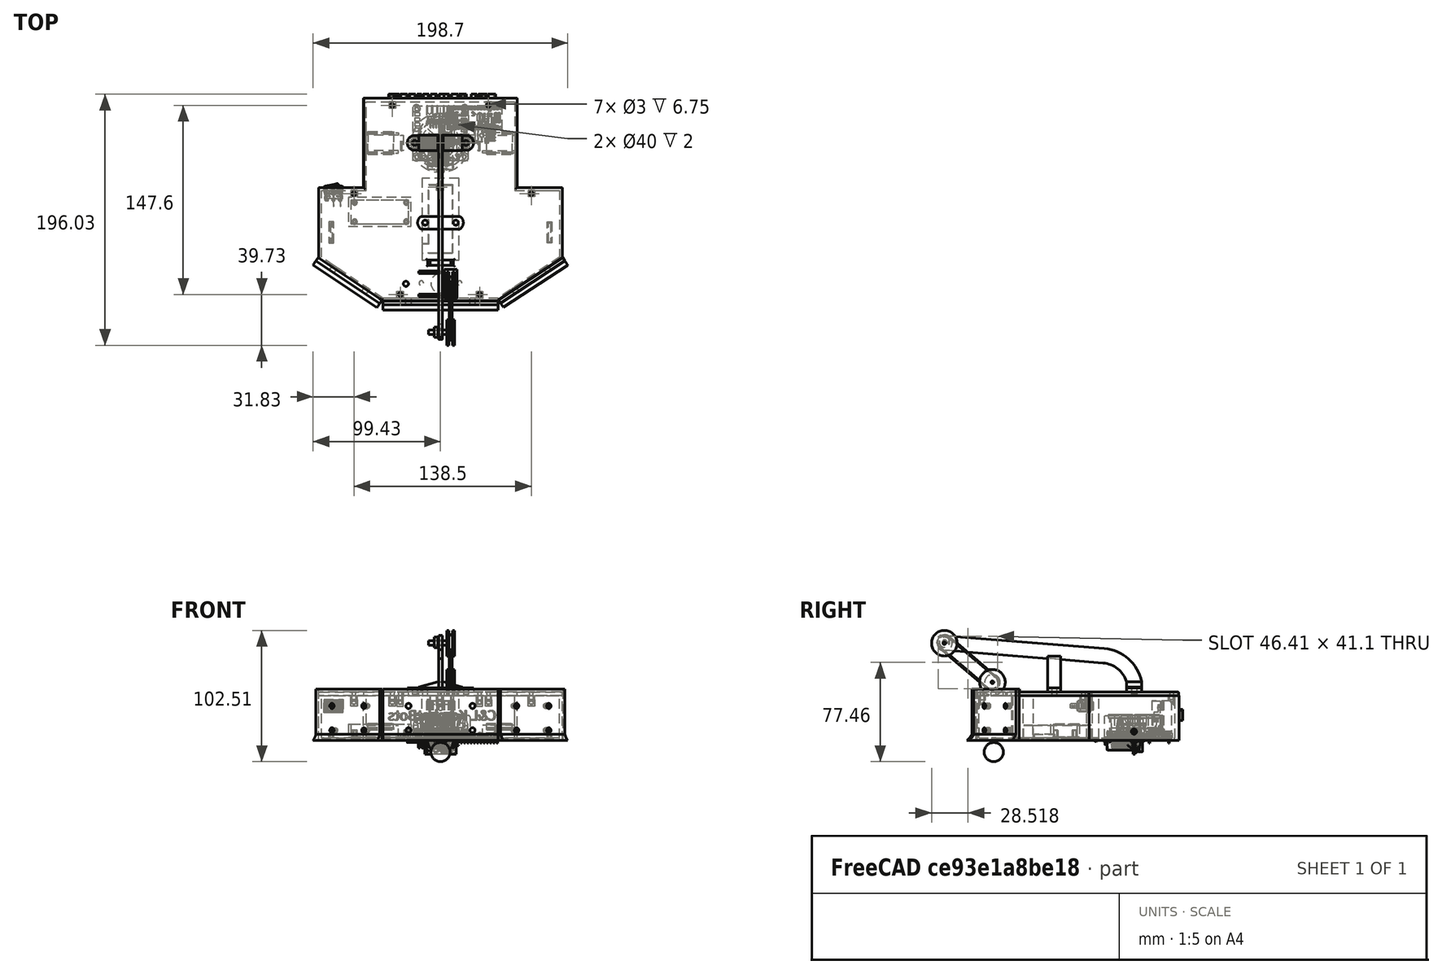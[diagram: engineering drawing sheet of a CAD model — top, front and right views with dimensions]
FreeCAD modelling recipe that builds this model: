
FCSTD DOCUMENT  (FreeCAD 0.20R29410 (Git))
Label: REALSIZEDrobot
License: Creative Commons Attribution-ShareAlike
LicenseURL: http://creativecommons.org/licenses/by-sa/4.0/
objects: Part::Feature×115, Part::Extrusion×50, Sketcher::SketchObject×41, Part::MultiFuse×25, Part::Cut×16, App::Part×9, Part::Chamfer×2, Mesh::Feature×2, Part::Fuse×1, Part::Sphere×1, Part::Part2DObjectPython×1, Part::Fillet×1
note: 253 computed .brp shape members not serialized (recipe doc carries the construction recipe); baked Part::Feature solids carry a one-line shape summary decoded from their .brp

FEATURE [Sketcher::SketchObject] Sketch
  FullyConstrained = true
  sketch-geometry (10):
    g0: LineSegment StartX=-60 StartY=35 StartZ=0 EndX=60 EndY=35 EndZ=0
    g1: LineSegment StartX=60 StartY=35 StartZ=0 EndX=60 EndY=-35 EndZ=0
    g2: LineSegment StartX=60 StartY=-35 StartZ=0 EndX=95 EndY=-35 EndZ=0
    g3: LineSegment StartX=95 StartY=-35 StartZ=0 EndX=95 EndY=-90 EndZ=0
    g4: LineSegment StartX=95 StartY=-90 StartZ=0 EndX=45 EndY=-123.166 EndZ=0
    g5: LineSegment StartX=45 StartY=-123.166 StartZ=0 EndX=-45 EndY=-123.166 EndZ=0
    g6: LineSegment StartX=-45 StartY=-123.166 StartZ=0 EndX=-95 EndY=-90 EndZ=0
    g7: LineSegment StartX=-95 StartY=-90 StartZ=0 EndX=-95 EndY=-35 EndZ=0
    g8: LineSegment StartX=-95 StartY=-35 StartZ=0 EndX=-60 EndY=-35 EndZ=0
    g9: LineSegment StartX=-60 StartY=-35 StartZ=0 EndX=-60 EndY=35 EndZ=0
  constraints (29):
    c: Horizontal(g0)
    c: Coincident(g0,g1)
    c: Vertical(g1)
    c: Coincident(g1,g2)
    c: Coincident(g2,g3)
    c: Coincident(g3,g4)
    c: Coincident(g4,g5)
    c: Coincident(g5,g6)
    c: Coincident(g6,g7)
    c: Coincident(g7,g8)
    c: Horizontal(g8)
    c: Coincident(g8,g9)
    c: Coincident(g9,g0)
    c: DistanceX(g0,g0) = 120
    c: Vertical(g9)
    c: DistanceY(g9,g9) = 70
    c: DistanceX(g8,g8) = 35
    c: Vertical(g7)
    c: DistanceX(g5,g5) = 90
    c: Horizontal(g5)
    c: Vertical(g3)
    c: DistanceY(g3,g3) = 55
    c: Horizontal(g2)
    c: Equal(g2,g8)
    c: Equal(g9,g1)
    c: Distance(g4) = 60
    c: Equal(g4,g6)
    c: Equal(g3,g7)
    c: Symmetric(g1,g0,g-1)
FEATURE [Part::Extrusion] Extrude  label="Floor"
  Base = -> Sketch
  Dir = (0,0,1)
  DirMode = 2
  FaceMakerClass = Part::FaceMakerBullseye
  LengthFwd = 2
  LengthRev = 0
  Solid = true
  Symmetric = false
FEATURE [Sketcher::SketchObject] Sketch001
  FullyConstrained = true
  sketch-geometry (22):
    g0: LineSegment StartX=-60 StartY=35 StartZ=0 EndX=60 EndY=35 EndZ=0
    g1: LineSegment StartX=60 StartY=35 StartZ=0 EndX=60 EndY=-35 EndZ=0
    g2: LineSegment StartX=60 StartY=-35 StartZ=0 EndX=95 EndY=-35 EndZ=0
    g3: LineSegment StartX=95 StartY=-35 StartZ=0 EndX=95 EndY=-90 EndZ=0
    g4: LineSegment StartX=95 StartY=-90 StartZ=0 EndX=45 EndY=-123.166 EndZ=0
    g5: LineSegment StartX=45 StartY=-123.166 StartZ=0 EndX=-45 EndY=-123.166 EndZ=0
    g6: LineSegment StartX=-45 StartY=-123.166 StartZ=0 EndX=-95 EndY=-90 EndZ=0
    g7: LineSegment StartX=-95 StartY=-90 StartZ=0 EndX=-95 EndY=-35 EndZ=0
    g8: LineSegment StartX=-95 StartY=-35 StartZ=0 EndX=-60 EndY=-35 EndZ=0
    g9: LineSegment StartX=-60 StartY=-35 StartZ=0 EndX=-60 EndY=35 EndZ=0
    g10: LineSegment StartX=-58 StartY=32 StartZ=0 EndX=58 EndY=32 EndZ=0
    g11: LineSegment StartX=58 StartY=32 StartZ=0 EndX=58 EndY=-37 EndZ=0
    g12: LineSegment StartX=58 StartY=-37 StartZ=0 EndX=93 EndY=-37 EndZ=0
    g13: LineSegment StartX=93 StartY=-37 StartZ=0 EndX=93 EndY=-89.3266 EndZ=0
    g14: LineSegment StartX=93 StartY=-89.3266 StartZ=0 EndX=45 EndY=-121.166 EndZ=0
    g15: LineSegment StartX=45 StartY=-121.166 StartZ=0 EndX=-45 EndY=-121.166 EndZ=0
    g16: LineSegment StartX=-45 StartY=-121.166 StartZ=0 EndX=-93 EndY=-89.3266 EndZ=0
    g17: LineSegment StartX=-93 StartY=-89.3266 StartZ=0 EndX=-93 EndY=-37 EndZ=0
    g18: LineSegment StartX=-93 StartY=-37 StartZ=0 EndX=-58 EndY=-37 EndZ=0
    g19: LineSegment StartX=-58 StartY=-37 StartZ=0 EndX=-58 EndY=32 EndZ=0
    g20: LineSegment StartX=-45 StartY=-121.166 StartZ=0 EndX=-45 EndY=-123.166 EndZ=0
    g21: LineSegment StartX=45 StartY=-121.166 StartZ=0 EndX=45 EndY=-123.166 EndZ=0
  constraints (63):
    c: Horizontal(g0)
    c: Coincident(g0,g1)
    c: Vertical(g1)
    c: Coincident(g1,g2)
    c: Horizontal(g2)
    c: Coincident(g2,g3)
    c: Vertical(g3)
    c: Coincident(g3,g4)
    c: Coincident(g4,g5)
    c: Horizontal(g5)
    c: Coincident(g5,g6)
    c: Coincident(g6,g7)
    c: Vertical(g7)
    c: Coincident(g7,g8)
    c: Horizontal(g8)
    c: Coincident(g8,g9)
    c: Coincident(g9,g0)
    c: Vertical(g9)
    c: Symmetric(g0,g1,g-1)
    c: DistanceX(g0,g0) = 120
    c: DistanceY(g1,g1) = 70
    c: Equal(g9,g1)
    c: DistanceX(g2,g2) = 35
    c: Equal(g2,g8)
    c: DistanceY(g3,g3) = 55
    c: DistanceX(g5,g5) = 90
    c: Distance(g4) = 60
    c: Equal(g4,g6)
    c: Equal(g3,g7)
    c: Horizontal(g10)
    c: Coincident(g11,g10)
    c: Vertical(g11)
    c: Coincident(g11,g12)
    c: Horizontal(g12)
    c: Coincident(g12,g13)
    c: Vertical(g13)
    c: Coincident(g13,g14)
    c: Coincident(g14,g15)
    c: Horizontal(g15)
    c: Coincident(g15,g16)
    c: Coincident(g16,g17)
    c: Vertical(g17)
    c: Coincident(g17,g18)
    c: Horizontal(g18)
    c: Coincident(g18,g19)
    c: Coincident(g19,g10)
    c: Vertical(g19)
    c: Distance(g10,g0) = 3
    c: Distance(g10,g9) = 2
    c: Distance(g17,g8) = 2
    c: Distance(g16,g7) = 2
    c: Distance(g15,g5) = 2
    c: Distance(g13,g3) = 2
    c: Distance(g12,g2) = 2
    c: Distance(g10,g1) = 2
    c: Coincident(g20,g15)
    c: Coincident(g20,g5)
    c: Coincident(g21,g14)
    c: Coincident(g21,g4)
    c: Vertical(g21)
    c: Vertical(g20)
    c: Parallel(g16,g6)
    c: Parallel(g14,g4)
FEATURE [Part::Extrusion] Extrude001  label="Walls"
  Base = -> Sketch001
  Dir = (0,0,1)
  DirMode = 2
  FaceMakerClass = Part::FaceMakerBullseye
  LengthFwd = 35
  LengthRev = 0
  Solid = true
  Symmetric = false
FEATURE [Part::MultiFuse] Fusion  label="Body"
  Refine = true
  Shapes = -> [Extrude001,Extrude]
FEATURE [Sketcher::SketchObject] Sketch002
  FullyConstrained = false
  MapMode = 5
  Placement = pos=(0,0,2) rot=(0,0,1;0rad)
  Support = -> [Fusion]
  sketch-geometry (36):
    g0: GeomPoint X=25 Y=0 Z=0
    g1: LineSegment StartX=33 StartY=6 StartZ=0 EndX=58 EndY=6 EndZ=0
    g2: LineSegment StartX=58 StartY=6 StartZ=0 EndX=58 EndY=8 EndZ=0
    g3: LineSegment StartX=58 StartY=8 StartZ=0 EndX=33 EndY=8 EndZ=0
    g4: LineSegment StartX=33 StartY=8 StartZ=0 EndX=33 EndY=6 EndZ=0
    g5: GeomPoint X=-25 Y=0 Z=0
    g6: LineSegment StartX=33 StartY=6 StartZ=0 EndX=25 EndY=0 EndZ=0
    g7: GeomPoint X=25 Y=0 Z=0
    g8: LineSegment StartX=32.5993 StartY=-6.5 StartZ=0 EndX=25 EndY=0 EndZ=0
    g9: GeomPoint X=-25 Y=0 Z=0
    g10: GeomPoint X=-25 Y=0 Z=0
    g11: GeomPoint X=25 Y=0 Z=0
    g12: LineSegment StartX=33 StartY=-6 StartZ=0 EndX=58 EndY=-6 EndZ=0
    g13: LineSegment StartX=58 StartY=-6 StartZ=0 EndX=58 EndY=-8 EndZ=0
    g14: LineSegment StartX=58 StartY=-8 StartZ=0 EndX=33 EndY=-8 EndZ=0
    g15: LineSegment StartX=33 StartY=-8 StartZ=0 EndX=33 EndY=-6 EndZ=0
    g16: LineSegment StartX=33 StartY=-6 StartZ=0 EndX=25 EndY=0 EndZ=0
    g17: GeomPoint X=25 Y=0 Z=0
    g18: LineSegment StartX=32.5993 StartY=6.5 StartZ=0 EndX=25 EndY=0 EndZ=0
    g19: GeomPoint X=-25 Y=0 Z=0
    g20: LineSegment StartX=-33 StartY=6 StartZ=0 EndX=-58 EndY=6 EndZ=0
    g21: LineSegment StartX=-58 StartY=6 StartZ=0 EndX=-58 EndY=8 EndZ=0
    g22: LineSegment StartX=-58 StartY=8 StartZ=0 EndX=-33 EndY=8 EndZ=0
    g23: LineSegment StartX=-33 StartY=8 StartZ=0 EndX=-33 EndY=6 EndZ=0
    g24: LineSegment StartX=-33 StartY=6 StartZ=0 EndX=-25 EndY=0 EndZ=0
    g25: GeomPoint X=-25 Y=0 Z=0
    g26: LineSegment StartX=-32.5993 StartY=-6.5 StartZ=0 EndX=-25 EndY=0 EndZ=0
    g27: GeomPoint X=-25 Y=0 Z=0
    g28: LineSegment StartX=-33 StartY=-6 StartZ=0 EndX=-58 EndY=-6 EndZ=0
    g29: LineSegment StartX=-58 StartY=-6 StartZ=0 EndX=-58 EndY=-8 EndZ=0
    g30: LineSegment StartX=-58 StartY=-8 StartZ=0 EndX=-33 EndY=-8 EndZ=0
    g31: LineSegment StartX=-33 StartY=-8 StartZ=0 EndX=-33 EndY=-6 EndZ=0
    g32: LineSegment StartX=-33 StartY=-6 StartZ=0 EndX=-25 EndY=0 EndZ=0
    g33: GeomPoint X=-25 Y=0 Z=0
    g34: LineSegment StartX=-32.5993 StartY=6.5 StartZ=0 EndX=-25 EndY=0 EndZ=0
    g35: LineSegment StartX=-33 StartY=8 StartZ=0 EndX=-33 EndY=-8 EndZ=0
  constraints (60):
    c: PointOnObject(g0,g-1)
    c: Distance(g-1,g0) = 25
    c: Coincident(g1,g2)
    c: Coincident(g2,g3)
    c: Coincident(g3,g4)
    c: Coincident(g4,g1)
    c: Horizontal(g1)
    c: Horizontal(g3)
    c: Vertical(g2)
    c: Vertical(g4)
    c: DistanceY(g4,g4) = 2
    c: DistanceX(g1,g1) = 25
    c: Coincident(g6,g1)
    c: Coincident(g6,g0)
    c: Distance(g6) = 10
    c: DistanceY(g-1,g1) = 6
    c: Coincident(g8,g7)
    c: Distance(g8) = 10
    c: Coincident(g12,g13)
    c: Coincident(g13,g14)
    c: Coincident(g14,g15)
    c: Coincident(g15,g12)
    c: Horizontal(g12)
    c: Horizontal(g14)
    c: Vertical(g13)
    c: Vertical(g15)
    c: Coincident(g16,g12)
    c: Coincident(g16,g11)
    c: Distance(g16) = 10
    c: Coincident(g18,g17)
    c: Distance(g18) = 10
    c: Coincident(g20,g21)
    c: Coincident(g21,g22)
    c: Coincident(g22,g23)
    c: Coincident(g23,g20)
    c: Horizontal(g20)
    c: Horizontal(g22)
    c: Vertical(g21)
    c: Vertical(g23)
    c: Coincident(g24,g20)
    c: Coincident(g24,g19)
    c: Distance(g24) = 10
    c: Coincident(g26,g25)
    c: Distance(g26) = 10
    c: Coincident(g28,g29)
    c: Coincident(g29,g30)
    c: Coincident(g30,g31)
    c: Coincident(g31,g28)
    c: Horizontal(g28)
    c: Horizontal(g30)
    c: Vertical(g29)
    c: Vertical(g31)
    c: Coincident(g32,g28)
    c: Coincident(g32,g27)
    c: Distance(g32) = 10
    c: Coincident(g34,g33)
    c: Distance(g34) = 10
    c: Coincident(g35,g22)
    c: Coincident(g35,g30)
    c: Vertical(g35)
FEATURE [Part::Extrusion] Extrude002  label="motorWalls"
  Base = -> Sketch002
  Dir = (0,0,1)
  DirMode = 2
  FaceMakerClass = Part::FaceMakerBullseye
  LengthFwd = 10
  LengthRev = 0
  Solid = true
  Symmetric = false
FEATURE [Sketcher::SketchObject] Sketch003
  FullyConstrained = false
  MapMode = 5
  Placement = pos=(0,0,2) rot=(0,0,1;0rad)
  Support = -> [Fusion]
  sketch-geometry (10):
    g0: LineSegment StartX=-31 StartY=6 StartZ=0 EndX=-29 EndY=6 EndZ=0
    g1: LineSegment StartX=-29 StartY=6 StartZ=0 EndX=-29 EndY=-6 EndZ=0
    g2: LineSegment StartX=-29 StartY=-6 StartZ=0 EndX=-31 EndY=-6 EndZ=0
    g3: LineSegment StartX=-31 StartY=-6 StartZ=0 EndX=-31 EndY=6 EndZ=0
    g4: GeomPoint X=-30 Y=0 Z=0
    g5: LineSegment StartX=31 StartY=6 StartZ=0 EndX=29 EndY=6 EndZ=0
    g6: LineSegment StartX=29 StartY=6 StartZ=0 EndX=29 EndY=-6 EndZ=0
    g7: LineSegment StartX=29 StartY=-6 StartZ=0 EndX=31 EndY=-6 EndZ=0
    g8: LineSegment StartX=31 StartY=-6 StartZ=0 EndX=31 EndY=6 EndZ=0
    g9: GeomPoint X=30 Y=0 Z=0
  constraints (22):
    c: Coincident(g0,g1)
    c: Coincident(g1,g2)
    c: Coincident(g2,g3)
    c: Coincident(g3,g0)
    c: Horizontal(g0)
    c: Horizontal(g2)
    c: Vertical(g1)
    c: Vertical(g3)
    c: PointOnObject(g4,g-1)
    c: Distance(g-1,g4) = 30
    c: Symmetric(g0,g2,g4)
    c: DistanceX(g0,g0) = 2
    c: DistanceY(g1,g1) = 12
    c: Coincident(g5,g6)
    c: Coincident(g6,g7)
    c: Coincident(g7,g8)
    c: Coincident(g8,g5)
    c: Horizontal(g5)
    c: Horizontal(g7)
    c: Vertical(g6)
    c: Vertical(g8)
    c: Symmetric(g5,g7,g9)
FEATURE [Part::Extrusion] Extrude003
  Base = -> Sketch003
  Dir = (0,0,1)
  DirMode = 2
  FaceMakerClass = Part::FaceMakerBullseye
  LengthFwd = 3
  LengthRev = 0
  Solid = true
  Symmetric = false
FEATURE [Part::Chamfer] Chamfer  label="MotorSlotter"
  Base = -> Extrude003
  Edges = 2 edges r=1: [Edge12,Edge24]
FEATURE [Part::MultiFuse] Fusion001  label="MotorHolders"
  Refine = true
  Shapes = -> [Chamfer,Extrude002]
FEATURE [Part::MultiFuse] Fusion002
  Refine = true
  Shapes = -> [Fusion001,Fusion]
FEATURE [Sketcher::SketchObject] Sketch004
  FullyConstrained = true
  MapMode = 5
  Placement = pos=(0,0,2) rot=(0,0,1;0rad)
  Support = -> [Fusion002]
  sketch-geometry (8):
    g0: Circle CenterX=-18.8 CenterY=26.75 CenterZ=0 NormalX=0 NormalY=0 NormalZ=1 AngleXU=0 Radius=3
    g1: Circle CenterX=-18.8 CenterY=26.75 CenterZ=0 NormalX=0 NormalY=0 NormalZ=1 AngleXU=0 Radius=1.5
    g2: Circle CenterX=18.8 CenterY=26.75 CenterZ=0 NormalX=0 NormalY=0 NormalZ=1 AngleXU=0 Radius=3
    g3: Circle CenterX=18.8 CenterY=26.75 CenterZ=0 NormalX=0 NormalY=0 NormalZ=1 AngleXU=0 Radius=1.5
    g4: Circle CenterX=18.8 CenterY=-11 CenterZ=0 NormalX=0 NormalY=0 NormalZ=1 AngleXU=0 Radius=3
    g5: Circle CenterX=18.8 CenterY=-11 CenterZ=0 NormalX=0 NormalY=0 NormalZ=1 AngleXU=0 Radius=1.5
    g6: Circle CenterX=-18.8 CenterY=-11 CenterZ=0 NormalX=0 NormalY=0 NormalZ=1 AngleXU=0 Radius=3
    g7: Circle CenterX=-18.8 CenterY=-11 CenterZ=0 NormalX=0 NormalY=0 NormalZ=1 AngleXU=0 Radius=1.5
  constraints (20):
    c: Coincident(g1,g0)
    c: Coincident(g3,g2)
    c: Coincident(g5,g4)
    c: Coincident(g7,g6)
    c: DistanceX(g-2,g6) = -18.8
    c: Diameter(g7) = 3
    c: Diameter(g6) = 6
    c: DistanceY(g-1,g6) = -11
    c: DistanceY(g-1,g4) = -11
    c: DistanceX(g-2,g4) = 18.8
    c: Diameter(g5) = 3
    c: Diameter(g4) = 6
    c: DistanceY(g-1,g2) = 26.75
    c: DistanceY(g-1,g0) = 26.75
    c: DistanceX(g-2,g2) = 18.8
    c: DistanceX(g-2,g0) = -18.8
    c: Diameter(g1) = 3
    c: Diameter(g0) = 6
    c: Diameter(g2) = 6
    c: Diameter(g3) = 3
FEATURE [Part::Feature] Part__Feature  label="L298N"
  Placement = pos=(21.5,29,6) rot=(1,0,0;1.5708rad)
  shape: bbox 43 x 43 x 25 mm, 410 faces (baked)
FEATURE [Part::Feature] Part__Feature001  label="Motor Case"
  shape: bbox 14 x 10 x 12 mm, 26 faces (baked)
FEATURE [Part::Feature] Part__Feature002  label="Rear Cover"
  Placement = pos=(7,0,0) rot=(0,0,1;0rad)
  shape: bbox 9 x 10 x 12 mm, 45 faces (baked)
FEATURE [Part::Feature] Part__Feature003  label="Rear Bearing"
  Placement = pos=(8.5,0,0) rot=(1,0,0;0.268142rad)
  shape: bbox 3 x 5 x 5 mm, 9 faces (baked)
FEATURE [Part::Feature] Part__Feature004  label="Front Bearing"
  Placement = pos=(-5.5,-1e-15,0) rot=(0,0,1;0rad)
  shape: bbox 1.5 x 4 x 4 mm, 6 faces (baked)
FEATURE [Part::Feature] Part__Feature005  label="Rotor"
  Placement = pos=(7,-3e-15,0) rot=(1,0,0;0.383419rad)
  shape: bbox 16.7 x 7.6 x 7.6 mm, 34 faces, 3 solids (baked)
FEATURE [Part::Feature] Part__Feature006  label="Spur 1-15_Spur01"
  Placement = pos=(-8.95,-3e-15,0) rot=(0.012886,0.999834,0.012886;1.57096rad)
  shape: bbox 1.5 x 3.391 x 3.382 mm, 38 faces (baked)
FEATURE [Part::Feature] Part__Feature007  label="Plate 1"
  Placement = pos=(-8,-6e-15,6e-15) rot=(0,1,0;1.5708rad)
  shape: bbox 1 x 10 x 12 mm, 14 faces (baked)
FEATURE [Part::Feature] Part__Feature008  label="Stand 2"
  Placement = pos=(-10,3.2,-3.6) rot=(0,0,1;0rad)
  shape: bbox 2 x 3 x 3 mm, 6 faces (baked)
FEATURE [Part::Feature] Part__Feature009  label="Stand 003"
  Placement = pos=(-10,-3.2,3.6) rot=(0,0,1;0rad)
  shape: bbox 2 x 3 x 3 mm, 6 faces (baked)
FEATURE [Part::Feature] Part__Feature010  label="Spur 2-24_Spur01"
  Placement = pos=(-8.95,2.21201,3.21201) rot=(0.153612,-0.976118,-0.153612;1.59497rad)
  shape: bbox 10.4 x 5.193 x 5.193 mm, 56 faces (baked)
FEATURE [Part::Feature] Part__Feature011  label="Plate 2"
  Placement = pos=(-11,-1.9e-14,5e-15) rot=(0,1,0;1.5708rad)
  shape: bbox 1 x 10 x 12 mm, 17 faces (baked)
FEATURE [Part::Feature] Part__Feature012  label="Spur 2-15_Spur01"
  Placement = pos=(-11.2,2.21201,3.21201) rot=(0.392285,0.832,0.392285;1.75369rad)
  shape: bbox 3 x 3.389 x 3.386 mm, 34 faces (baked)
FEATURE [Part::Feature] Part__Feature013  label="Spur 1-26_Spur01"
  Placement = pos=(-11.95,-0.153707,-0.136628) rot=(-0.467826,-0.749852,0.467826;1.85478rad)
  shape: bbox 4.2 x 5.587 x 5.6 mm, 60 faces (baked)
FEATURE [Part::Feature] Part__Feature014  label="Spur 1-15_Spur002"
  Placement = pos=(-13.45,-0.153707,-0.136628) rot=(-0.575214,0.581599,-0.575214;2.08803rad)
  shape: bbox 1.5 x 3.378 x 3.392 mm, 38 faces (baked)
FEATURE [Part::Feature] Part__Feature015  label="Stand 4"
  Placement = pos=(-16.1,3.2,-3.6) rot=(-1,0,0;1.00084rad)
  shape: bbox 5.1 x 3 x 3 mm, 6 faces (baked)
FEATURE [Part::Feature] Part__Feature016  label="Stand 004"
  Placement = pos=(-16.1,-3.2,3.6) rot=(1,0,0;1.52971rad)
  shape: bbox 5.1 x 3 x 3 mm, 6 faces (baked)
FEATURE [Part::Feature] Part__Feature017  label="Spur 1-24_Spur01"
  Placement = pos=(-13.45,-2.35559,-3.35559) rot=(-0.550538,0.627547,-0.550538;2.02074rad)
  shape: bbox 7.1 x 5.2 x 5.2 mm, 56 faces (baked)
FEATURE [Part::Feature] Part__Feature018  label="Plate 3"
  Placement = pos=(-16.1,-2.1e-14,5e-15) rot=(0.707107,0,-0.707107;3.14159rad)
  shape: bbox 2 x 10.2 x 12 mm, 29 faces (baked)
FEATURE [Part::Feature] Part__Feature019  label="Spur 1-15_Spur003"
  Placement = pos=(-15.15,-2.35559,-3.35559) rot=(0.659293,0.361476,0.659293;2.44787rad)
  shape: bbox 1.5 x 3.389 x 3.386 mm, 38 faces (baked)
FEATURE [Part::Feature] Part__Feature020  label="Spur 2-26_Spur01"
  Placement = pos=(-15.15,-2.7e-14,5e-15) rot=(0.080265,0.993537,0.080265;1.57728rad)
  shape: bbox 11.5 x 5.592 x 5.599 mm, 59 faces (baked)
FEATURE [Part::Feature] Part__Feature021  label="countersunk flat head cross recess screw_iso_ISO 7046-1 - M2 x 12 - Z --- 12N"
  Placement = pos=(-17.4,-3.2,3.6) rot=(1,0,0;0.036509rad)
  shape: bbox 12 x 3.8 x 3.8 mm, 41 faces (baked)
FEATURE [Part::Feature] Part__Feature022  label="countersunk flat head cross recess screw_iso_ISO 7046-1 - M2 x 12 - Z --- 12N001"
  Placement = pos=(-17.4,3.2,-3.6) rot=(1,0,0;1.44457rad)
  shape: bbox 12 x 3.8 x 3.8 mm, 41 faces (baked)
FEATURE [App::Part] GA12_N20_Motor_Complet  label="Left Motor"
  Group = -> [Part__Feature001,Part__Feature002,Part__Feature003,Part__Feature004,Part__Feature005,Part__Feature006,Part__Feature007,Part__Feature008,Part__Feature009,Part__Feature010,Part__Feature011,Part__Feature012,Part__Feature013,Part__Feature014,Part__Feature015,Part__Feature016,Part__Feature017,Part__Feature018,Part__Feature019,Part__Feature020,Part__Feature021,Part__Feature022]
  Origin = -> Origin
  Placement = pos=(40,-7.2e-15,7) rot=(0,0.707107,0.707107;3.14159rad)
FEATURE [Part::Feature] Part__Feature023  label="Motor Case001"
  shape: bbox 14 x 10 x 12 mm, 26 faces (baked)
FEATURE [Part::Feature] Part__Feature024  label="Rear Cover001"
  Placement = pos=(7,0,0) rot=(0,0,1;0rad)
  shape: bbox 9 x 10 x 12 mm, 45 faces (baked)
FEATURE [Part::Feature] Part__Feature025  label="Rear Bearing001"
  Placement = pos=(8.5,0,0) rot=(1,0,0;0.268142rad)
  shape: bbox 3 x 5 x 5 mm, 9 faces (baked)
FEATURE [Part::Feature] Part__Feature026  label="Front Bearing001"
  Placement = pos=(-5.5,-1e-15,0) rot=(0,0,1;0rad)
  shape: bbox 1.5 x 4 x 4 mm, 6 faces (baked)
FEATURE [Part::Feature] Part__Feature027  label="Rotor001"
  Placement = pos=(7,-3e-15,0) rot=(1,0,0;0.383419rad)
  shape: bbox 16.7 x 7.6 x 7.6 mm, 34 faces, 3 solids (baked)
FEATURE [Part::Feature] Part__Feature028  label="Spur 1-15_Spur004"
  Placement = pos=(-8.95,-3e-15,0) rot=(0.012886,0.999834,0.012886;1.57096rad)
  shape: bbox 1.5 x 3.391 x 3.382 mm, 38 faces (baked)
FEATURE [Part::Feature] Part__Feature029  label="Plate 004"
  Placement = pos=(-8,-6e-15,6e-15) rot=(0,1,0;1.5708rad)
  shape: bbox 1 x 10 x 12 mm, 14 faces (baked)
FEATURE [Part::Feature] Part__Feature030  label="Stand 005"
  Placement = pos=(-10,3.2,-3.6) rot=(0,0,1;0rad)
  shape: bbox 2 x 3 x 3 mm, 6 faces (baked)
FEATURE [Part::Feature] Part__Feature031  label="Stand 006"
  Placement = pos=(-10,-3.2,3.6) rot=(0,0,1;0rad)
  shape: bbox 2 x 3 x 3 mm, 6 faces (baked)
FEATURE [Part::Feature] Part__Feature032  label="Spur 2-24_Spur002"
  Placement = pos=(-8.95,2.21201,3.21201) rot=(0.153612,-0.976118,-0.153612;1.59497rad)
  shape: bbox 10.4 x 5.193 x 5.193 mm, 56 faces (baked)
FEATURE [Part::Feature] Part__Feature033  label="Plate 005"
  Placement = pos=(-11,-1.9e-14,5e-15) rot=(0,1,0;1.5708rad)
  shape: bbox 1 x 10 x 12 mm, 17 faces (baked)
FEATURE [Part::Feature] Part__Feature034  label="Spur 2-15_Spur002"
  Placement = pos=(-11.2,2.21201,3.21201) rot=(0.392285,0.832,0.392285;1.75369rad)
  shape: bbox 3 x 3.389 x 3.386 mm, 34 faces (baked)
FEATURE [Part::Feature] Part__Feature035  label="Spur 1-26_Spur002"
  Placement = pos=(-11.95,-0.153707,-0.136628) rot=(-0.467826,-0.749852,0.467826;1.85478rad)
  shape: bbox 4.2 x 5.587 x 5.6 mm, 60 faces (baked)
FEATURE [Part::Feature] Part__Feature036  label="Spur 1-15_Spur005"
  Placement = pos=(-13.45,-0.153707,-0.136628) rot=(-0.575214,0.581599,-0.575214;2.08803rad)
  shape: bbox 1.5 x 3.378 x 3.392 mm, 38 faces (baked)
FEATURE [Part::Feature] Part__Feature037  label="Stand 007"
  Placement = pos=(-16.1,3.2,-3.6) rot=(-1,0,0;1.00084rad)
  shape: bbox 5.1 x 3 x 3 mm, 6 faces (baked)
FEATURE [Part::Feature] Part__Feature038  label="Stand 008"
  Placement = pos=(-16.1,-3.2,3.6) rot=(1,0,0;1.52971rad)
  shape: bbox 5.1 x 3 x 3 mm, 6 faces (baked)
FEATURE [Part::Feature] Part__Feature039  label="Spur 1-24_Spur002"
  Placement = pos=(-13.45,-2.35559,-3.35559) rot=(-0.550538,0.627547,-0.550538;2.02074rad)
  shape: bbox 7.1 x 5.2 x 5.2 mm, 56 faces (baked)
FEATURE [Part::Feature] Part__Feature040  label="Plate 006"
  Placement = pos=(-16.1,-2.1e-14,5e-15) rot=(0.707107,0,-0.707107;3.14159rad)
  shape: bbox 2 x 10.2 x 12 mm, 29 faces (baked)
FEATURE [Part::Feature] Part__Feature041  label="Spur 1-15_Spur006"
  Placement = pos=(-15.15,-2.35559,-3.35559) rot=(0.659293,0.361476,0.659293;2.44787rad)
  shape: bbox 1.5 x 3.389 x 3.386 mm, 38 faces (baked)
FEATURE [Part::Feature] Part__Feature042  label="Spur 2-26_Spur002"
  Placement = pos=(-15.15,-2.7e-14,5e-15) rot=(0.080265,0.993537,0.080265;1.57728rad)
  shape: bbox 11.5 x 5.592 x 5.599 mm, 59 faces (baked)
FEATURE [Part::Feature] Part__Feature043  label="countersunk flat head cross recess screw_iso_ISO 7046-1 - M2 x 12 - Z --- 12N002"
  Placement = pos=(-17.4,-3.2,3.6) rot=(1,0,0;0.036509rad)
  shape: bbox 12 x 3.8 x 3.8 mm, 41 faces (baked)
FEATURE [Part::Feature] Part__Feature044  label="countersunk flat head cross recess screw_iso_ISO 7046-1 - M2 x 12 - Z --- 12N003"
  Placement = pos=(-17.4,3.2,-3.6) rot=(1,0,0;1.44457rad)
  shape: bbox 12 x 3.8 x 3.8 mm, 41 faces (baked)
FEATURE [App::Part] GA12_N20_Motor_Complet001  label="Right Motor"
  Group = -> [Part__Feature023,Part__Feature024,Part__Feature025,Part__Feature026,Part__Feature027,Part__Feature028,Part__Feature029,Part__Feature030,Part__Feature031,Part__Feature032,Part__Feature033,Part__Feature034,Part__Feature035,Part__Feature036,Part__Feature037,Part__Feature038,Part__Feature039,Part__Feature040,Part__Feature041,Part__Feature042,Part__Feature043,Part__Feature044]
  Origin = -> Origin001
  Placement = pos=(-40,-1.5e-14,7) rot=(1,0,0;1.5708rad)
FEATURE [Part::Extrusion] Extrude004  label="L289N Holder"
  Base = -> Sketch004
  Dir = (0,0,1)
  DirMode = 2
  FaceMakerClass = Part::FaceMakerBullseye
  LengthFwd = 4
  LengthRev = 0
  Solid = true
  Symmetric = false
FEATURE [Part::MultiFuse] Fusion003
  Refine = true
  Shapes = -> [Extrude004,Fusion002]
FEATURE [Sketcher::SketchObject] Sketch005
  FullyConstrained = true
  MapMode = 5
  Placement = pos=(60,0,0) rot=(0.57735,0.57735,0.57735;2.0944rad)
  Support = -> [Fusion003]
  sketch-geometry (1):
    g0: Circle CenterX=0 CenterY=7 CenterZ=0 NormalX=0 NormalY=0 NormalZ=1 AngleXU=0 Radius=2
  constraints (3):
    c: PointOnObject(g0,g-2)
    c: Diameter(g0) = 4
    c: Distance(g0,g-1) = 7
FEATURE [Sketcher::SketchObject] Sketch006
  FullyConstrained = true
  MapMode = 5
  Placement = pos=(-60,0,0) rot=(0.57735,-0.57735,-0.57735;2.0944rad)
  Support = -> [Fusion003]
  sketch-geometry (1):
    g0: Circle CenterX=0 CenterY=7 CenterZ=0 NormalX=0 NormalY=0 NormalZ=1 AngleXU=0 Radius=2
  constraints (3):
    c: PointOnObject(g0,g-2)
    c: Diameter(g0) = 4
    c: Distance(g-1,g0) = 7
FEATURE [Part::Extrusion] Extrude005
  Base = -> Sketch005
  Dir = (1,0,0)
  DirMode = 2
  FaceMakerClass = Part::FaceMakerBullseye
  LengthFwd = 10
  LengthRev = 0
  Solid = true
  Symmetric = true
FEATURE [Part::Extrusion] Extrude006
  Base = -> Sketch006
  Dir = (-1,0,0)
  DirMode = 2
  FaceMakerClass = Part::FaceMakerBullseye
  LengthFwd = 10
  LengthRev = 0
  Solid = true
  Symmetric = true
FEATURE [Part::MultiFuse] Fusion004  label="Motor Gaps"
  Refine = true
  Shapes = -> [Extrude005,Extrude006]
FEATURE [Part::Cut] Cut
  Base = -> Fusion003
  Refine = true
  Tool = -> Fusion004
FEATURE [Part::Feature] Part__Feature045  label="INTERRUPTOR BASCULANTE"
  Placement = pos=(-83.5,-33.5,27) rot=(0.57735,-0.57735,-0.57735;4.18879rad)
  shape: bbox 15.1 x 17.9 x 10.42 mm, 555 faces, 4 solids (baked)
FEATURE [Sketcher::SketchObject] Sketch007
  FullyConstrained = false
  MapMode = 5
  Placement = pos=(0,-35,0) rot=(0,0.707107,0.707107;3.14159rad)
  Support = -> [Cut]
  sketch-geometry (4):
    g0: LineSegment StartX=90.8327 StartY=31.6367 StartZ=0 EndX=76.0827 EndY=31.6367 EndZ=0
    g1: LineSegment StartX=76.0827 StartY=31.6367 StartZ=0 EndX=76.0827 EndY=21.8867 EndZ=0
    g2: LineSegment StartX=76.0827 StartY=21.8867 StartZ=0 EndX=90.8327 EndY=21.8867 EndZ=0
    g3: LineSegment StartX=90.8327 StartY=21.8867 StartZ=0 EndX=90.8327 EndY=31.6367 EndZ=0
  constraints (8):
    c: Coincident(g0,g1)
    c: Coincident(g1,g2)
    c: Coincident(g2,g3)
    c: Coincident(g3,g0)
    c: Horizontal(g0)
    c: Horizontal(g2)
    c: Vertical(g1)
    c: Vertical(g3)
FEATURE [Part::Extrusion] Extrude007  label="InterruptGap"
  Base = -> Sketch007
  Dir = (0,1,-2e-16)
  DirMode = 2
  FaceMakerClass = Part::FaceMakerBullseye
  LengthFwd = 10
  LengthRev = 0
  Solid = true
  Symmetric = true
FEATURE [Part::Cut] Cut001
  Base = -> Cut
  Refine = true
  Tool = -> Extrude007
FEATURE [Sketcher::SketchObject] Sketch008
  FullyConstrained = false
  MapMode = 5
  Placement = pos=(0,0,2) rot=(0,0,1;0rad)
  Support = -> [Cut001]
  sketch-geometry (20):
    g0: LineSegment StartX=83.4 StartY=-61.75 StartZ=0 EndX=87 EndY=-61.75 EndZ=0
    g1: LineSegment StartX=87 StartY=-61.75 StartZ=0 EndX=87 EndY=-78.25 EndZ=0
    g2: LineSegment StartX=87 StartY=-78.25 StartZ=0 EndX=83.4 EndY=-78.25 EndZ=0
    g3: LineSegment StartX=83.4 StartY=-78.25 StartZ=0 EndX=83.4 EndY=-61.75 EndZ=0
    g4: LineSegment StartX=84.4 StartY=-62.6 StartZ=0 EndX=86 EndY=-62.6 EndZ=0
    g5: LineSegment StartX=86 StartY=-62.6 StartZ=0 EndX=86 EndY=-77.4 EndZ=0
    g6: LineSegment StartX=86 StartY=-77.4 StartZ=0 EndX=84.4 EndY=-77.4 EndZ=0
    g7: LineSegment StartX=84.4 StartY=-77.4 StartZ=0 EndX=84.4 EndY=-62.6 EndZ=0
    g8: GeomPoint X=93 Y=-70 Z=0
    g9: LineSegment StartX=-0.686599 StartY=-70 StartZ=0 EndX=93 EndY=-70 EndZ=0
    g10: LineSegment StartX=-83.4 StartY=-61.75 StartZ=0 EndX=-87 EndY=-61.75 EndZ=0
    g11: LineSegment StartX=-87 StartY=-61.75 StartZ=0 EndX=-87 EndY=-78.25 EndZ=0
    g12: LineSegment StartX=-87 StartY=-78.25 StartZ=0 EndX=-83.4 EndY=-78.25 EndZ=0
    g13: LineSegment StartX=-83.4 StartY=-78.25 StartZ=0 EndX=-83.4 EndY=-61.75 EndZ=0
    g14: LineSegment StartX=-84.4 StartY=-62.6 StartZ=0 EndX=-86 EndY=-62.6 EndZ=0
    g15: LineSegment StartX=-86 StartY=-62.6 StartZ=0 EndX=-86 EndY=-77.4 EndZ=0
    g16: LineSegment StartX=-86 StartY=-77.4 StartZ=0 EndX=-84.4 EndY=-77.4 EndZ=0
    g17: LineSegment StartX=-84.4 StartY=-77.4 StartZ=0 EndX=-84.4 EndY=-62.6 EndZ=0
    g18: GeomPoint X=-93 Y=-70 Z=0
    g19: LineSegment StartX=0.686599 StartY=-70 StartZ=0 EndX=-93 EndY=-70 EndZ=0
  constraints (46):
    c: Coincident(g0,g1)
    c: Coincident(g1,g2)
    c: Coincident(g2,g3)
    c: Coincident(g3,g0)
    c: Horizontal(g0)
    c: Horizontal(g2)
    c: Vertical(g1)
    c: Vertical(g3)
    c: Coincident(g4,g5)
    c: Coincident(g5,g6)
    c: Coincident(g6,g7)
    c: Coincident(g7,g4)
    c: Horizontal(g4)
    c: Horizontal(g6)
    c: Vertical(g7)
    c: DistanceX(g-2,g8) = 93
    c: DistanceY(g-1,g8) = -70
    c: Distance(g8,g1) = 6
    c: Coincident(g9,g8)
    c: Symmetric(g1,g0,g9)
    c: DistanceY(g1,g1) = 16.5
    c: Symmetric(g4,g5,g9)
    c: DistanceY(g5,g5) = 14.8
    c: DistanceX(g0,g0) = 3.6
    c: DistanceX(g4,g4) = 1.6
    c: Distance(g4,g1) = 1
    c: Coincident(g10,g11)
    c: Coincident(g11,g12)
    c: Coincident(g12,g13)
    c: Coincident(g13,g10)
    c: Horizontal(g10)
    c: Horizontal(g12)
    c: Vertical(g11)
    c: Vertical(g13)
    c: Coincident(g14,g15)
    c: Coincident(g15,g16)
    c: Coincident(g16,g17)
    c: Coincident(g17,g14)
    c: Horizontal(g14)
    c: Horizontal(g16)
    c: Vertical(g17)
    c: Distance(g18,g11) = 6
    c: Coincident(g19,g18)
    c: Symmetric(g11,g10,g19)
    c: Symmetric(g14,g15,g19)
    c: Distance(g14,g11) = 1
FEATURE [Part::Extrusion] Extrude008  label="HitSensorHolders"
  Base = -> Sketch008
  Dir = (0,0,1)
  DirMode = 2
  FaceMakerClass = Part::FaceMakerBullseye
  LengthFwd = 3
  LengthRev = 0
  Solid = true
  Symmetric = false
FEATURE [Part::MultiFuse] Fusion005
  Refine = true
  Shapes = -> [Cut001,Extrude008]
FEATURE [Part::Feature] Part__Feature050  label="BAttery"
  Placement = pos=(0,-59.5,2) rot=(0,0,1;0rad)
  shape: bbox 23 x 53 x 10 mm, 8 faces (baked)
FEATURE [Sketcher::SketchObject] Sketch009
  FullyConstrained = true
  sketch-geometry (11):
    g0: LineSegment StartX=-14.5 StartY=-78.5 StartZ=0 EndX=-9.5 EndY=-78.5 EndZ=0
    g1: LineSegment StartX=-9.5 StartY=-78.5 StartZ=0 EndX=-9.5 EndY=-32.5 EndZ=0
    g2: LineSegment StartX=-9.5 StartY=-32.5 StartZ=0 EndX=9.5 EndY=-32.5 EndZ=0
    g3: LineSegment StartX=9.5 StartY=-32.5 StartZ=0 EndX=9.5 EndY=-86.5 EndZ=0
    g4: LineSegment StartX=9.5 StartY=-86.5 StartZ=0 EndX=-14.5 EndY=-86.5 EndZ=0
    g5: LineSegment StartX=-14.5 StartY=-86.5 StartZ=0 EndX=-14.5 EndY=-91.5 EndZ=0
    g6: LineSegment StartX=-14.5 StartY=-91.5 StartZ=0 EndX=14.5 EndY=-91.5 EndZ=0
    g7: LineSegment StartX=14.5 StartY=-91.5 StartZ=0 EndX=14.5 EndY=-27.5 EndZ=0
    g8: LineSegment StartX=14.5 StartY=-27.5 StartZ=0 EndX=-14.5 EndY=-27.5 EndZ=0
    g9: LineSegment StartX=-14.5 StartY=-27.5 StartZ=0 EndX=-14.5 EndY=-78.5 EndZ=0
    g10: GeomPoint X=0 Y=-59.5 Z=0
  constraints (30):
    c: Horizontal(g0)
    c: Coincident(g0,g1)
    c: Vertical(g1)
    c: Coincident(g1,g2)
    c: Horizontal(g2)
    c: Coincident(g2,g3)
    c: Vertical(g3)
    c: Coincident(g3,g4)
    c: Horizontal(g4)
    c: Coincident(g4,g5)
    c: Vertical(g5)
    c: Coincident(g5,g6)
    c: Horizontal(g6)
    c: Coincident(g6,g7)
    c: Vertical(g7)
    c: Coincident(g7,g8)
    c: Horizontal(g8)
    c: Coincident(g8,g9)
    c: Coincident(g9,g0)
    c: Vertical(g9)
    c: DistanceX(g2,g2) = 19
    c: PointOnObject(g10,g-2)
    c: DistanceY(g10,g-1) = 59.5
    c: Symmetric(g3,g1,g10)
    c: Symmetric(g6,g8,g10)
    c: DistanceX(g8,g8) = 29
    c: DistanceY(g3,g3) = 54
    c: DistanceY(g7,g7) = 64
    c: DistanceY(g1,g1) = 46
    c: DistanceX(g6,g6) = 29
FEATURE [Part::Extrusion] Extrude009  label="Battery Gap"
  Base = -> Sketch009
  Dir = (0,0,1)
  DirMode = 2
  FaceMakerClass = Part::FaceMakerBullseye
  LengthFwd = 35
  LengthRev = 0
  Solid = true
  Symmetric = false
FEATURE [Part::MultiFuse] Fusion006
  Refine = true
  Shapes = -> [Extrude009,Fusion005]
FEATURE [Part::Feature] Part__Feature051  label="Arduino Nano"
  Placement = pos=(8.85506,11.9484,3.8e-15) rot=(0,0,1;0rad)
  shape: bbox 43.18 x 18 x 6.8 mm, 962 faces (baked)
FEATURE [Part::Feature] Part__Feature052  label="Mini USB"
  Placement = pos=(8.54506,19.5727,4.14) rot=(0,0,1;0rad)
  shape: bbox 9.5 x 9.7 x 3.9 mm, 197 faces (baked)
FEATURE [Part::Feature] Part__Feature053  label="ATMEGA328P-AU--3DModel-STEP-56544.step.STEP.STEP.STEP"
  Placement = pos=(2.81625,4.09996,0.676804) rot=(1,0,0;1.5708rad)
  shape: bbox 9 x 9 x 1.2 mm, 650 faces, 33 solids (baked)
FEATURE [App::Part] ATMEGA328P_AU_STEP  label="ATMEGA328P-AU.STEP"
  Group = -> [Part__Feature053]
  Origin = -> Origin004
  Placement = pos=(19.8219,24.4243,4.0882) rot=(0,0,1;3.92699rad)
FEATURE [Part::Feature] Part__Feature054  label="CSTCE Crystal"
  Placement = pos=(25.8562,23.1047,4.15) rot=(0,0,-1;0.785398rad)
  shape: bbox 3.182 x 3.182 x 0.71 mm, 47 faces (baked)
FEATURE [Part::Feature] Part__Feature055  label="2Pin Tactile Switch 6x3.6"
  Placement = pos=(30.7142,19.8184,4.14) rot=(0,0,1;1.5708rad)
  shape: bbox 3.633 x 7.9 x 2.2 mm, 48 faces (baked)
FEATURE [Part::Feature] Part__Feature056  label="0603 Resistor"
  Placement = pos=(34.4251,22.4184,4.14) rot=(0,0,1;0rad)
  shape: bbox 1.6 x 0.8 x 0.5 mm, 69 faces (baked)
FEATURE [Part::Feature] Part__Feature057  label="0603 Resistor001"
  Placement = pos=(34.4251,20.7184,4.14) rot=(0,0,1;0rad)
  shape: bbox 1.6 x 0.8 x 0.5 mm, 69 faces (baked)
FEATURE [Part::Feature] Part__Feature058  label="0603 Resistor002"
  Placement = pos=(34.4251,18.9184,4.14) rot=(0,0,1;0rad)
  shape: bbox 1.6 x 0.8 x 0.5 mm, 69 faces (baked)
FEATURE [Part::Feature] Part__Feature059  label="0603 Resistor003"
  Placement = pos=(34.4251,17.2184,4.14) rot=(0,0,1;0rad)
  shape: bbox 1.6 x 0.8 x 0.5 mm, 69 faces (baked)
FEATURE [Part::Feature] Part__Feature060  label="Blue LED"
  Placement = pos=(37.0251,22.4184,4.14) rot=(0,0,1;0rad)
  shape: bbox 1.6 x 0.8 x 0.6 mm, 19 faces (baked)
FEATURE [Part::Feature] Part__Feature061  label="Green LED"
  Placement = pos=(37.0251,20.7184,4.14) rot=(0,0,1;0rad)
  shape: bbox 1.6 x 0.8 x 0.6 mm, 19 faces (baked)
FEATURE [Part::Feature] Part__Feature062  label="Red LED"
  Placement = pos=(37.0251,18.9184,4.14) rot=(0,0,1;0rad)
  shape: bbox 1.6 x 0.8 x 0.6 mm, 19 faces (baked)
FEATURE [Part::Feature] Part__Feature063  label="Blue LED001"
  Placement = pos=(37.0251,17.2184,4.14) rot=(0,0,1;0rad)
  shape: bbox 1.6 x 0.8 x 0.6 mm, 19 faces (baked)
FEATURE [Part::Feature] Part__Feature064  label="Header 2x3"
  Placement = pos=(45.6765,17.0321,4.14) rot=(0,0,1;1.5708rad)
  shape: bbox 5.075 x 7.615 x 10 mm, 168 faces, 6 solids (baked)
FEATURE [Part::Feature] Part__Feature065  label="SOT89"
  Placement = pos=(38.4751,17.3184,0.94) rot=(0,0,1;1.5708rad)
  shape: bbox 7.1 x 6.5 x 1.6 mm, 80 faces (baked)
FEATURE [Part::Feature] Part__Feature066  label="1206 Tantalum"
  Placement = pos=(38.6251,22.3684,2.54) rot=(0,1,0;3.14159rad)
  shape: bbox 3.2 x 1.6 x 1.5 mm, 24 faces (baked)
FEATURE [Part::Feature] Part__Feature067  label="0603 Resistor004"
  Placement = pos=(38.4251,24.9684,2.54) rot=(0,1,0;3.14159rad)
  shape: bbox 1.6 x 0.8 x 0.5 mm, 69 faces (baked)
FEATURE [Part::Feature] Part__Feature068  label="0603 Capacitor"
  Placement = pos=(35.0338,14.4684,2.54) rot=(0,1,0;3.14159rad)
  shape: bbox 1.6 x 0.8 x 0.7 mm, 69 faces (baked)
FEATURE [Part::Feature] Part__Feature069  label="1206 Tantalum001"
  Placement = pos=(7.64506,24.3684,2.54) rot=(1,0,0;3.14159rad)
  shape: bbox 3.2 x 1.6 x 1.5 mm, 24 faces (baked)
FEATURE [Part::Feature] Part__Feature070  label="0603 Capacitor001"
  Placement = pos=(6.90589,22.4745,2.54) rot=(0,1,0;3.14159rad)
  shape: bbox 1.6 x 0.8 x 0.7 mm, 69 faces (baked)
FEATURE [Part::Feature] Part__Feature071  label="0603 Capacitor002"
  Placement = pos=(17.8451,14.0245,2.54) rot=(0,1,0;3.14159rad)
  shape: bbox 1.6 x 0.8 x 0.7 mm, 69 faces (baked)
FEATURE [Part::Feature] Part__Feature072  label="0603 Capacitor003"
  Placement = pos=(17.8451,15.0767,2.54) rot=(0,1,0;3.14159rad)
  shape: bbox 1.6 x 0.8 x 0.7 mm, 69 faces (baked)
FEATURE [Part::Feature] Part__Feature073  label="0603 Capacitor004"
  Placement = pos=(25.3451,21.2855,2.54) rot=(0,1,0;3.14159rad)
  shape: bbox 1.6 x 0.8 x 0.7 mm, 69 faces (baked)
FEATURE [Part::Feature] Part__Feature074  label="0603 Resistor005"
  Placement = pos=(23.8451,15.8601,2.54) rot=(0,1,0;3.14159rad)
  shape: bbox 1.6 x 0.8 x 0.5 mm, 69 faces (baked)
FEATURE [Part::Feature] Part__Feature075  label="0603 Resistor006"
  Placement = pos=(23.8451,14.4709,2.54) rot=(0,1,0;3.14159rad)
  shape: bbox 1.6 x 0.8 x 0.5 mm, 69 faces (baked)
FEATURE [Part::Feature] Part__Feature076  label="CSTCE Crystal001"
  Placement = pos=(13.1731,14.7184,2.53) rot=(0,1,0;3.14159rad)
  shape: bbox 3.2 x 1.35 x 0.71 mm, 47 faces (baked)
FEATURE [Part::Feature] Part__Feature077  label="SOIC16"
  Placement = pos=(16.6451,19.5642,2.54) rot=(0,1,0;3.14159rad)
  shape: bbox 10.2 x 6 x 1.5 mm, 154 faces (baked)
FEATURE [App::Part] Arduino_Nano  label="Arduino Nano001"
  Group = -> [Part__Feature051,Part__Feature052,ATMEGA328P_AU_STEP,Part__Feature054,Part__Feature055,Part__Feature056,Part__Feature057,Part__Feature058,Part__Feature059,Part__Feature060,Part__Feature061,Part__Feature062,Part__Feature063,Part__Feature064,Part__Feature065,Part__Feature066,Part__Feature067,Part__Feature068,Part__Feature069,Part__Feature070,Part__Feature071,Part__Feature072,Part__Feature073,+4 more]
  Origin = -> Origin005
  Placement = pos=(-73.5,-34.5,12.5) rot=(1,0,0;3.14159rad)
FEATURE [Sketcher::SketchObject] Sketch010
  FullyConstrained = false
  MapMode = 5
  Placement = pos=(0,0,2) rot=(0,0,1;0rad)
  Support = -> [Fusion006]
  sketch-geometry (13):
    g0: LineSegment StartX=-52.8 StartY=-54 StartZ=0 EndX=0 EndY=-54 EndZ=0
    g1: LineSegment StartX=-52.8 StartY=-54 StartZ=0 EndX=-84.748 EndY=-54 EndZ=0
    g2: Circle CenterX=-66.9946 CenterY=-46.5 CenterZ=0 NormalX=0 NormalY=0 NormalZ=1 AngleXU=0 Radius=1
    g3: Circle CenterX=-66.9946 CenterY=-46.5 CenterZ=0 NormalX=0 NormalY=0 NormalZ=1 AngleXU=0 Radius=2
    g4: Circle CenterX=-66.9946 CenterY=-61.5 CenterZ=0 NormalX=0 NormalY=0 NormalZ=1 AngleXU=0 Radius=1
    g5: Circle CenterX=-66.9946 CenterY=-61.5 CenterZ=0 NormalX=0 NormalY=0 NormalZ=1 AngleXU=0 Radius=2
    g6: GeomPoint X=-25.3 Y=-54 Z=0
    g7: Circle CenterX=-26.6711 CenterY=-46.5 CenterZ=0 NormalX=0 NormalY=0 NormalZ=1 AngleXU=0 Radius=1
    g8: Circle CenterX=-26.6711 CenterY=-46.5 CenterZ=0 NormalX=0 NormalY=0 NormalZ=1 AngleXU=0 Radius=2
    g9: Circle CenterX=-26.6711 CenterY=-61.5 CenterZ=0 NormalX=0 NormalY=0 NormalZ=1 AngleXU=0 Radius=1
    g10: Circle CenterX=-26.6711 CenterY=-61.5 CenterZ=0 NormalX=0 NormalY=0 NormalZ=1 AngleXU=0 Radius=2
    g11: LineSegment StartX=-52.8 StartY=-54 StartZ=0 EndX=0 EndY=-54 EndZ=0
    g12: GeomPoint X=-25.3 Y=-54 Z=0
  constraints (24):
    c: DistanceY(g0,g-1) = 54
    c: PointOnObject(g0,g-2)
    c: Horizontal(g0)
    c: Coincident(g1,g0)
    c: Horizontal(g1)
    c: Coincident(g3,g2)
    c: Diameter(g2) = 2
    c: Diameter(g3) = 4
    c: Distance(g2,g1) = 7.5
    c: Coincident(g5,g4)
    c: Diameter(g4) = 2
    c: Diameter(g5) = 4
    c: PointOnObject(g6,g0)
    c: DistanceX(g6,g-1) = 25.3
    c: Coincident(g8,g7)
    c: Diameter(g7) = 2
    c: Diameter(g8) = 4
    c: Distance(g7,g0) = 7.5
    c: Horizontal(g11)
    c: PointOnObject(g12,g11)
    c: Coincident(g10,g9)
    c: Diameter(g9) = 2
    c: Diameter(g10) = 4
    c: Distance(g9,g11) = 7.5
FEATURE [Part::Extrusion] Extrude010  label="Arduino Holder"
  Base = -> Sketch010
  Dir = (0,0,1)
  DirMode = 2
  FaceMakerClass = Part::FaceMakerBullseye
  LengthFwd = 6
  LengthRev = 0
  Solid = true
  Symmetric = false
FEATURE [Part::MultiFuse] Fusion007
  Refine = true
  Shapes = -> [Fusion006,Extrude010]
FEATURE [Sketcher::SketchObject] Sketch011
  FullyConstrained = true
  MapMode = 5
  Placement = pos=(0,-91.5,0) rot=(1,0,0;1.5708rad)
  Support = -> [Extrude009]
  sketch-geometry (10):
    g0: LineSegment StartX=8 StartY=35 StartZ=0 EndX=10 EndY=35 EndZ=0
    g1: LineSegment StartX=10 StartY=35 StartZ=0 EndX=10 EndY=2 EndZ=0
    g2: LineSegment StartX=10 StartY=2 StartZ=0 EndX=-10 EndY=2 EndZ=0
    g3: LineSegment StartX=-10 StartY=2 StartZ=0 EndX=-10 EndY=35 EndZ=0
    g4: LineSegment StartX=-10 StartY=35 StartZ=0 EndX=-8 EndY=35 EndZ=0
    g5: LineSegment StartX=-8 StartY=35 StartZ=0 EndX=-8 EndY=4 EndZ=0
    g6: LineSegment StartX=-8 StartY=4 StartZ=0 EndX=8 EndY=4 EndZ=0
    g7: LineSegment StartX=8 StartY=4 StartZ=0 EndX=8 EndY=35 EndZ=0
    g8: GeomPoint X=0 Y=2 Z=0
    g9: LineSegment StartX=0 StartY=2 StartZ=0 EndX=0 EndY=0 EndZ=0
  constraints (28):
    c: Horizontal(g0)
    c: Coincident(g0,g1)
    c: Vertical(g1)
    c: Coincident(g1,g2)
    c: Coincident(g2,g3)
    c: Vertical(g3)
    c: Coincident(g3,g4)
    c: Horizontal(g4)
    c: Coincident(g4,g5)
    c: Vertical(g5)
    c: Coincident(g5,g6)
    c: Horizontal(g6)
    c: Coincident(g6,g7)
    c: Coincident(g7,g0)
    c: Vertical(g7)
    c: DistanceX(g0,g0) = 2
    c: Equal(g4,g0)
    c: DistanceX(g6,g6) = 16
    c: DistanceY(g1,g1) = 33
    c: Equal(g3,g1)
    c: Distance(g6,g2) = 2
    c: Horizontal(g2)
    c: PointOnObject(g8,g2)
    c: DistanceX(g8,g1) = 10
    c: DistanceY(g-1,g1) = 2
    c: Coincident(g9,g8)
    c: Coincident(g9,g-1)
    c: Vertical(g9)
FEATURE [Part::Feature] Part__Feature078  label="Varsayılan"
  shape: bbox 42.6 x 16.1 x 5.9 mm, 343 faces, 7 solids (baked)
FEATURE [App::Part] f818e014b189db61e14b8aa713db12f520221103_1_5sl1wb  label="Bluetooth Module"
  Group = -> [Part__Feature078]
  Origin = -> Origin006
  Placement = pos=(-8,-93,41) rot=(-0.57735,-0.57735,0.57735;4.18879rad)
FEATURE [Part::Extrusion] Extrude011  label="Bluetooth Module Holder"
  Base = -> Sketch011
  Dir = (0,-1,2e-16)
  DirMode = 2
  FaceMakerClass = Part::FaceMakerBullseye
  LengthFwd = 4
  LengthRev = 0
  Solid = true
  Symmetric = false
FEATURE [Part::MultiFuse] Fusion008
  Refine = true
  Shapes = -> [Fusion007,Extrude011]
FEATURE [Sketcher::SketchObject] Sketch012
  FullyConstrained = false
  MapMode = 5
  Placement = pos=(4.907e-13,3.136e-13,35) rot=(0,0,1;0rad)
  Support = -> [Fusion008]
  sketch-geometry (8):
    g0: LineSegment StartX=8 StartY=-92.5 StartZ=0 EndX=8.5 EndY=-92.5 EndZ=0
    g1: LineSegment StartX=8.5 StartY=-92.5 StartZ=0 EndX=8.5 EndY=-94.7 EndZ=0
    g2: LineSegment StartX=8.5 StartY=-94.7 StartZ=0 EndX=8 EndY=-94.7 EndZ=0
    g3: LineSegment StartX=8 StartY=-94.7 StartZ=0 EndX=8 EndY=-92.5 EndZ=0
    g4: LineSegment StartX=-8 StartY=-92.5 StartZ=0 EndX=-8.5 EndY=-92.5 EndZ=0
    g5: LineSegment StartX=-8.5 StartY=-92.5 StartZ=0 EndX=-8.5 EndY=-94.7 EndZ=0
    g6: LineSegment StartX=-8.5 StartY=-94.7 StartZ=0 EndX=-8 EndY=-94.7 EndZ=0
    g7: LineSegment StartX=-8 StartY=-94.7 StartZ=0 EndX=-8 EndY=-92.5 EndZ=0
  constraints (20):
    c: Coincident(g0,g1)
    c: Coincident(g1,g2)
    c: Coincident(g2,g3)
    c: Coincident(g3,g0)
    c: Horizontal(g0)
    c: Horizontal(g2)
    c: Vertical(g1)
    c: Vertical(g3)
    c: DistanceY(g1,g1) = 2.2
    c: DistanceX(g0,g0) = 0.5
    c: DistanceX(g-2,g0) = 8
    c: DistanceY(g-1,g0) = -92.5
    c: Coincident(g4,g5)
    c: Coincident(g5,g6)
    c: Coincident(g6,g7)
    c: Coincident(g7,g4)
    c: Horizontal(g4)
    c: Horizontal(g6)
    c: Vertical(g5)
    c: Vertical(g7)
FEATURE [Part::Extrusion] Extrude012  label="Bluetooth Module Slotter"
  Base = -> Sketch012
  Dir = (1.4e-14,9e-15,1)
  DirMode = 2
  FaceMakerClass = Part::FaceMakerBullseye
  LengthFwd = -32
  LengthRev = 0
  Solid = true
  Symmetric = false
FEATURE [Part::Cut] Cut002
  Base = -> Fusion008
  Refine = true
  Tool = -> Extrude012
FEATURE [Sketcher::SketchObject] Sketch013
  FullyConstrained = false
  MapMode = 5
  Placement = pos=(0,-37,0) rot=(1,0,0;1.5708rad)
  Support = -> [Cut002]
  sketch-geometry (4):
    g0: LineSegment StartX=-91.0267 StartY=31.7549 StartZ=0 EndX=-86.0267 EndY=31.7549 EndZ=0
    g1: LineSegment StartX=-86.0267 StartY=31.7549 StartZ=0 EndX=-86.0267 EndY=26.7549 EndZ=0
    g2: LineSegment StartX=-86.0267 StartY=26.7549 StartZ=0 EndX=-91.0267 EndY=26.7549 EndZ=0
    g3: LineSegment StartX=-91.0267 StartY=26.7549 StartZ=0 EndX=-91.0267 EndY=31.7549 EndZ=0
  constraints (10):
    c: Coincident(g0,g1)
    c: Coincident(g1,g2)
    c: Coincident(g2,g3)
    c: Coincident(g3,g0)
    c: Horizontal(g0)
    c: Horizontal(g2)
    c: Vertical(g1)
    c: Vertical(g3)
    c: DistanceX(g0,g0) = 5
    c: DistanceY(g1,g1) = 5
FEATURE [Part::Extrusion] Extrude013
  Base = -> Sketch013
  Dir = (0,-1,2e-16)
  DirMode = 2
  FaceMakerClass = Part::FaceMakerBullseye
  LengthFwd = 5
  LengthRev = 0
  Solid = true
  Symmetric = false
FEATURE [Part::Chamfer] Chamfer001  label="Bot Screw Holder"
  Base = -> Extrude013
  Edges = 1 edges r=4.99: [Edge10]
FEATURE [Sketcher::SketchObject] Sketch014
  FullyConstrained = true
  MapMode = 5
  Placement = pos=(0,7e-15,31.7549) rot=(0,0,1;0rad)
  Support = -> [Chamfer001]
  sketch-geometry (1):
    g0: Circle CenterX=-88.6 CenterY=-39.7 CenterZ=0 NormalX=0 NormalY=0 NormalZ=1 AngleXU=0 Radius=1.5
  constraints (3):
    c: Diameter(g0) = 3
    c: DistanceX(g-2,g0) = -88.6
    c: DistanceY(g-1,g0) = -39.7
FEATURE [Part::Extrusion] Extrude014  label="Screw Hole"
  Base = -> Sketch014
  Dir = (0,2e-16,1)
  DirMode = 2
  FaceMakerClass = Part::FaceMakerBullseye
  LengthFwd = -8
  LengthRev = 0
  Placement = pos=(0,0,4.5) rot=(0,0,1;0rad)
  Solid = true
  Symmetric = false
FEATURE [Sketcher::SketchObject] Sketch015
  FullyConstrained = false
  MapMode = 5
  Placement = pos=(0,7e-15,31.7549) rot=(0,0,1;0rad)
  Support = -> [Chamfer001]
  sketch-geometry (4):
    g0: LineSegment StartX=-91.0267 StartY=-37 StartZ=0 EndX=-86.0267 EndY=-37 EndZ=0
    g1: LineSegment StartX=-86.0267 StartY=-37 StartZ=0 EndX=-86.0267 EndY=-42 EndZ=0
    g2: LineSegment StartX=-86.0267 StartY=-42 StartZ=0 EndX=-91.0267 EndY=-42 EndZ=0
    g3: LineSegment StartX=-91.0267 StartY=-42 StartZ=0 EndX=-91.0267 EndY=-37 EndZ=0
  constraints (10):
    c: Coincident(g0,g1)
    c: Coincident(g1,g2)
    c: Coincident(g2,g3)
    c: Coincident(g3,g0)
    c: Horizontal(g0)
    c: Horizontal(g2)
    c: Vertical(g1)
    c: Vertical(g3)
    c: DistanceY(g1,g1) = 5
    c: DistanceX(g2,g2) = 5
FEATURE [Part::Extrusion] Extrude015  label="Top Screw Holder"
  Base = -> Sketch015
  Dir = (0,2e-16,1)
  DirMode = 2
  FaceMakerClass = Part::FaceMakerBullseye
  LengthFwd = 3.25
  LengthRev = 0
  Solid = true
  Symmetric = false
FEATURE [Part::Fuse] Fusion009
  Base = -> Chamfer001
  Refine = true
  Tool = -> Extrude015
FEATURE [Part::Cut] Cut003  label="Lid Screw Hole"
  Base = -> Fusion009
  Placement = pos=(21,0,0) rot=(0,0,1;0rad)
  Refine = true
  Tool = -> Extrude014
FEATURE [Part::Feature] Part__Feature079  label="Lid Screw Hole001"
  Placement = pos=(159.5,0,0) rot=(0,0,1;0rad)
  shape: bbox 5 x 5 x 8.25 mm, 13 faces (baked)
FEATURE [Part::Feature] Part__Feature080  label="Lid Screw Hole002"
  Placement = pos=(51,69,0) rot=(0,0,1;0rad)
  shape: bbox 5 x 5 x 8.25 mm, 13 faces (baked)
FEATURE [Part::Feature] Part__Feature081  label="Lid Screw Hole003"
  Placement = pos=(126,69,0) rot=(0,0,1;0rad)
  shape: bbox 5 x 5 x 8.25 mm, 13 faces (baked)
FEATURE [Part::Feature] Part__Feature082  label="Lid Screw Hole004"
  Placement = pos=(-120,-158,0) rot=(0,0,1;3.14159rad)
  shape: bbox 5 x 5 x 8.25 mm, 13 faces (baked)
FEATURE [Part::Feature] Part__Feature083  label="Lid Screw Hole005"
  Placement = pos=(-58,-158,0) rot=(0,0,1;3.14159rad)
  shape: bbox 5 x 5 x 8.25 mm, 13 faces (baked)
FEATURE [Part::Feature] Part__Feature084  label="Lid Screw Hole006"
  Placement = pos=(88,5,0) rot=(0,0,1;0rad)
  shape: bbox 5 x 5 x 8.25 mm, 13 faces (baked)
FEATURE [Part::MultiFuse] Fusion010  label="Lid Screw Holes"
  Refine = true
  Shapes = -> [Cut003,Part__Feature079,Part__Feature080,Part__Feature081,Part__Feature082,Part__Feature083,Part__Feature084]
FEATURE [Part::MultiFuse] Fusion011
  Refine = true
  Shapes = -> [Cut002,Fusion010]
FEATURE [Sketcher::SketchObject] Sketch016
  FullyConstrained = false
  MapMode = 5
  Placement = pos=(70.4856,-106.261,0) rot=(0.919866,0.27735,0.27735;1.65423rad)
  Support = -> [Fusion011]
  sketch-geometry (4):
    g0: Circle CenterX=15 CenterY=27 CenterZ=0 NormalX=0 NormalY=0 NormalZ=1 AngleXU=0 Radius=2
    g1: Circle CenterX=15 CenterY=8 CenterZ=0 NormalX=0 NormalY=0 NormalZ=1 AngleXU=0 Radius=2
    g2: Circle CenterX=-15 CenterY=27 CenterZ=0 NormalX=0 NormalY=0 NormalZ=1 AngleXU=0 Radius=2
    g3: Circle CenterX=-15 CenterY=8 CenterZ=0 NormalX=0 NormalY=0 NormalZ=1 AngleXU=0 Radius=2
  constraints (9):
    c: Diameter(g1) = 4
    c: Diameter(g0) = 4
    c: DistanceX(g-2,g0) = 15
    c: DistanceX(g-2,g1) = 15
    c: Distance(g1,g0) = 19
    c: DistanceY(g-1,g1) = 8
    c: Diameter(g3) = 4
    c: Diameter(g2) = 4
    c: Distance(g3,g2) = 19
FEATURE [Part::Extrusion] Extrude016
  Base = -> Sketch016
  Dir = (0.552771,-0.833333,-5e-16)
  DirMode = 2
  FaceMakerClass = Part::FaceMakerBullseye
  LengthFwd = 10
  LengthRev = 0
  Solid = true
  Symmetric = true
FEATURE [Sketcher::SketchObject] Sketch017
  FullyConstrained = false
  MapMode = 5
  Placement = pos=(-70.4856,-106.261,0) rot=(0.919866,-0.27735,-0.27735;1.65423rad)
  Support = -> [Fusion011]
  sketch-geometry (4):
    g0: Circle CenterX=-15 CenterY=8 CenterZ=0 NormalX=0 NormalY=0 NormalZ=1 AngleXU=0 Radius=2
    g1: Circle CenterX=-15 CenterY=27 CenterZ=0 NormalX=0 NormalY=0 NormalZ=1 AngleXU=0 Radius=2
    g2: Circle CenterX=15 CenterY=8 CenterZ=0 NormalX=0 NormalY=0 NormalZ=1 AngleXU=0 Radius=2
    g3: Circle CenterX=15 CenterY=27 CenterZ=0 NormalX=0 NormalY=0 NormalZ=1 AngleXU=0 Radius=2
  constraints (9):
    c: Diameter(g1) = 4
    c: Distance(g1,g0) = 19
    c: DistanceY(g-1,g0) = 8
    c: DistanceX(g-2,g0) = -15
    c: DistanceX(g-2,g1) = -15
    c: Diameter(g0) = 4
    c: Diameter(g3) = 4
    c: Distance(g3,g2) = 19
    c: Diameter(g2) = 4
FEATURE [Part::Extrusion] Extrude017
  Base = -> Sketch017
  Dir = (-0.552771,-0.833333,0)
  DirMode = 2
  FaceMakerClass = Part::FaceMakerBullseye
  LengthFwd = 10
  LengthRev = 0
  Solid = true
  Symmetric = true
FEATURE [Sketcher::SketchObject] Sketch018
  FullyConstrained = false
  MapMode = 5
  Placement = pos=(0,-123.166,0) rot=(1,0,0;1.5708rad)
  Support = -> [Fusion011]
  sketch-geometry (4):
    g0: Circle CenterX=-25 CenterY=27 CenterZ=0 NormalX=0 NormalY=0 NormalZ=1 AngleXU=0 Radius=2
    g1: Circle CenterX=-25 CenterY=8 CenterZ=0 NormalX=0 NormalY=0 NormalZ=1 AngleXU=0 Radius=2
    g2: Circle CenterX=25 CenterY=27 CenterZ=0 NormalX=0 NormalY=0 NormalZ=1 AngleXU=0 Radius=2
    g3: Circle CenterX=25 CenterY=8 CenterZ=0 NormalX=0 NormalY=0 NormalZ=1 AngleXU=0 Radius=2
  constraints (9):
    c: Equal(g0,g1)
    c: Diameter(g0) = 4
    c: DistanceY(g-1,g1) = 8
    c: Distance(g1,g0) = 19
    c: DistanceX(g-2,g1) = -25
    c: DistanceX(g-2,g0) = -25
    c: Equal(g2,g3)
    c: Diameter(g2) = 4
    c: Distance(g3,g2) = 19
FEATURE [Part::Extrusion] Extrude018
  Base = -> Sketch018
  Dir = (0,-1,2e-16)
  DirMode = 2
  FaceMakerClass = Part::FaceMakerBullseye
  LengthFwd = 10
  LengthRev = 0
  Solid = true
  Symmetric = true
FEATURE [Part::MultiFuse] Fusion012  label="HitPlankScrewHoles"
  Refine = true
  Shapes = -> [Extrude017,Extrude018,Extrude016]
FEATURE [Part::Cut] Cut004  label="Robot Body"
  Base = -> Fusion011
  Refine = true
  Tool = -> Fusion012
FEATURE [Part::Feature] Part__Feature085  label="Center Hit Plank"
  Placement = pos=(-45,-125,20) rot=(0,0,1;0rad)
  shape: bbox 90 x 7 x 40 mm, 11 faces (baked)
FEATURE [Part::Feature] Part__Feature086  label="Right Hit Plank"
  Placement = pos=(46.0783,-123.812,20) rot=(0,0,1;0.580322rad)
  shape: bbox 54.02 x 38.75 x 40 mm, 11 faces (baked)
FEATURE [Part::Feature] Part__Feature087  label="Left Hit Plank"
  Placement = pos=(-96.3708,-90.6732,20) rot=(0,0,-1;0.589049rad)
  shape: bbox 53.78 x 39.15 x 40 mm, 11 faces (baked)
FEATURE [Sketcher::SketchObject] Sketch019
  FullyConstrained = true
  MapMode = 5
  Placement = pos=(0,5.9e-15,26.7549) rot=(1,0,0;3.14159rad)
  Support = -> [Cut004]
  sketch-geometry (4):
    g0: LineSegment StartX=36 StartY=10 StartZ=0 EndX=56 EndY=10 EndZ=0
    g1: LineSegment StartX=56 StartY=10 StartZ=0 EndX=56 EndY=8 EndZ=0
    g2: LineSegment StartX=56 StartY=8 StartZ=0 EndX=36 EndY=8 EndZ=0
    g3: LineSegment StartX=36 StartY=8 StartZ=0 EndX=36 EndY=10 EndZ=0
  constraints (12):
    c: Coincident(g0,g1)
    c: Coincident(g1,g2)
    c: Coincident(g2,g3)
    c: Coincident(g3,g0)
    c: Horizontal(g0)
    c: Horizontal(g2)
    c: Vertical(g1)
    c: Vertical(g3)
    c: DistanceY(g-1,g1) = 8
    c: DistanceY(g1,g1) = 2
    c: DistanceX(g2,g2) = 20
    c: DistanceX(g-2,g2) = 36
FEATURE [Part::Extrusion] Extrude019  label="Motor Holders Lid Slot"
  Base = -> Sketch019
  Dir = (0,-2e-16,-1)
  DirMode = 2
  FaceMakerClass = Part::FaceMakerBullseye
  LengthFwd = 2
  LengthRev = 0
  Placement = pos=(0,1,0) rot=(0,0,1;0rad)
  Solid = true
  Symmetric = false
  TaperAngle = -3
FEATURE [Part::Extrusion] Extrude020  label="Motor Holders Lid Slot001"
  Base = -> Sketch019
  Dir = (0,-2e-16,-1)
  DirMode = 2
  FaceMakerClass = Part::FaceMakerBullseye
  LengthFwd = 2
  LengthRev = 0
  Placement = pos=(-92,17,0) rot=(0,0,1;0rad)
  Solid = true
  Symmetric = false
  TaperAngle = -3
FEATURE [Part::Extrusion] Extrude021  label="Motor Holders Lid Slot002"
  Base = -> Sketch019
  Dir = (0,-2e-16,-1)
  DirMode = 2
  FaceMakerClass = Part::FaceMakerBullseye
  LengthFwd = 2
  LengthRev = 0
  Placement = pos=(0,17,0) rot=(0,0,1;0rad)
  Solid = true
  Symmetric = false
  TaperAngle = -3
FEATURE [Part::Extrusion] Extrude022  label="Motor Holders Lid Slot003"
  Base = -> Sketch019
  Dir = (0,-2e-16,-1)
  DirMode = 2
  FaceMakerClass = Part::FaceMakerBullseye
  LengthFwd = 2
  LengthRev = 0
  Placement = pos=(-92,1,0) rot=(0,0,1;0rad)
  Solid = true
  Symmetric = false
  TaperAngle = -3
FEATURE [Part::MultiFuse] Fusion013  label="Motor Lid Gaps"
  Refine = true
  Shapes = -> [Extrude019,Extrude020,Extrude021,Extrude022]
FEATURE [Part::Cut] Cut005
  Base = -> Cut004
  Refine = true
  Tool = -> Fusion013
FEATURE [Part::Feature] Part__Feature088  label="Left Motor Lid"
  Placement = pos=(-56.5,0,2.5) rot=(0,0,1;0rad)
  shape: bbox 20 x 18 x 5.1 mm, 18 faces (baked)
FEATURE [Part::Feature] Part__Feature089  label="Right Motor Lid"
  Placement = pos=(36,0,2.5) rot=(0,0,1;0rad)
  shape: bbox 20 x 18 x 5.1 mm, 18 faces (baked)
FEATURE [Sketcher::SketchObject] Sketch020
  FullyConstrained = true
  MapMode = 5
  Placement = pos=(0,2.25e-14,31.7549) rot=(1,0,0;3.14159rad)
  Support = -> [Cut005]
  sketch-geometry (8):
    g0: LineSegment StartX=-70 StartY=-44.9 StartZ=0 EndX=-25 EndY=-44.9 EndZ=0
    g1: LineSegment StartX=-25 StartY=-44.9 StartZ=0 EndX=-25 EndY=-63.3 EndZ=0
    g2: LineSegment StartX=-25 StartY=-63.3 StartZ=0 EndX=-70 EndY=-63.3 EndZ=0
    g3: LineSegment StartX=-70 StartY=-63.3 StartZ=0 EndX=-70 EndY=-44.9 EndZ=0
    g4: LineSegment StartX=-72 StartY=-42.9 StartZ=0 EndX=-23 EndY=-42.9 EndZ=0
    g5: LineSegment StartX=-23 StartY=-42.9 StartZ=0 EndX=-23 EndY=-65.3 EndZ=0
    g6: LineSegment StartX=-23 StartY=-65.3 StartZ=0 EndX=-72 EndY=-65.3 EndZ=0
    g7: LineSegment StartX=-72 StartY=-65.3 StartZ=0 EndX=-72 EndY=-42.9 EndZ=0
  constraints (24):
    c: Coincident(g0,g1)
    c: Coincident(g1,g2)
    c: Coincident(g2,g3)
    c: Coincident(g3,g0)
    c: Horizontal(g0)
    c: Horizontal(g2)
    c: Vertical(g1)
    c: Vertical(g3)
    c: Coincident(g4,g5)
    c: Coincident(g5,g6)
    c: Coincident(g6,g7)
    c: Coincident(g7,g4)
    c: Horizontal(g4)
    c: Horizontal(g6)
    c: Vertical(g5)
    c: Vertical(g7)
    c: Distance(g1,g5) = 2
    c: Distance(g1,g6) = 2
    c: Distance(g0,g4) = 2
    c: DistanceY(g-1,g0) = -44.9
    c: DistanceX(g-2,g0) = -25
    c: DistanceX(g0,g0) = 45
    c: DistanceY(g1,g1) = 18.4
    c: Distance(g0,g7) = 2
FEATURE [Part::Extrusion] Extrude023  label="Arduino Walls"
  Base = -> Sketch020
  Dir = (0,-7e-16,-1)
  DirMode = 2
  FaceMakerClass = Part::FaceMakerBullseye
  LengthFwd = 10
  LengthRev = 0
  Placement = pos=(0,-108,-19) rot=(0,0,1;0rad)
  Solid = true
  Symmetric = false
FEATURE [Part::MultiFuse] Fusion014  label="Full Robot Body"
  Refine = true
  Shapes = -> [Cut005,Extrude023]
FEATURE [Part::Sphere] Sphere  label="Marble"
  Angle1 = -90
  Angle2 = 90
  Angle3 = 360
  AttacherType = Attacher::AttachEngine3D
  Placement = pos=(0,-109.5,-9) rot=(0,0,1;0rad)
  Radius = 7.5
FEATURE [Mesh::Feature] Brilliant_Snicket__1_  label="Caster Marble Holder"
  Placement = pos=(-45,-110,4.88e-14) rot=(-1,0,0;3.14159rad)
FEATURE [Sketcher::SketchObject] Sketch024
  FullyConstrained = false
  MapMode = 5
  Placement = pos=(0,0,2) rot=(0,0,1;0rad)
  Support = -> [Fusion014]
  sketch-geometry (2):
    g0: Circle CenterX=15.0092 CenterY=-109.45 CenterZ=0 NormalX=0 NormalY=0 NormalZ=1 AngleXU=0 Radius=1.75
    g1: Circle CenterX=-15.0092 CenterY=-109.45 CenterZ=0 NormalX=0 NormalY=0 NormalZ=1 AngleXU=0 Radius=1.75
  constraints (2):
    c: Diameter(g0) = 3.5
    c: Diameter(g1) = 3.5
FEATURE [Part::Extrusion] Extrude024  label="Idle Wheel Base Screw Hole"
  Base = -> Sketch024
  Dir = (0,0,1)
  DirMode = 2
  FaceMakerClass = Part::FaceMakerBullseye
  LengthFwd = 10
  LengthRev = 0
  Solid = true
  Symmetric = true
FEATURE [Part::Cut] Cut006
  Base = -> Fusion014
  Refine = true
  Tool = -> Extrude024
FEATURE [Part::Part2DObjectPython] ShapeString  # Draft 2D object (typed FeaturePython)
  FontFile = <path>
  MakeFace = true
  Placement = pos=(43.52,35,15.82) rot=(0,0.707107,0.707107;3.14159rad)
  Size = 5
  String = C&L KombatBots
  Tracking = 0
FEATURE [Part::Extrusion] Extrude025  label="RobotText"
  Base = -> ShapeString
  Dir = (1e-16,1,4e-16)
  DirMode = 2
  FaceMakerClass = Part::FaceMakerBullseye
  LengthFwd = 3
  LengthRev = 0
  Solid = false
  Symmetric = false
FEATURE [Part::MultiFuse] Fusion015  label="Full Robot Body001"
  Refine = true
  Shapes = -> [Cut006,Extrude025]
FEATURE [Sketcher::SketchObject] Sketch025
  FullyConstrained = false
  MapMode = 5
  Placement = pos=(0,0,35) rot=(0,0,1;0rad)
  Support = -> [Fusion015]
  sketch-geometry (21):
    g0: LineSegment StartX=-59.987 StartY=34.8273 StartZ=0 EndX=59.8041 EndY=34.8273 EndZ=0
    g1: LineSegment StartX=59.8041 StartY=34.8273 StartZ=0 EndX=59.8041 EndY=-34.9668 EndZ=0
    g2: LineSegment StartX=59.8041 StartY=-34.9668 StartZ=0 EndX=94.9993 EndY=-34.9668 EndZ=0
    g3: LineSegment StartX=94.9993 StartY=-34.9668 StartZ=0 EndX=94.9993 EndY=-89.9973 EndZ=0
    g4: LineSegment StartX=94.9993 StartY=-89.9973 StartZ=0 EndX=44.9644 EndY=-123.178 EndZ=0
    g5: LineSegment StartX=44.9644 StartY=-123.178 StartZ=0 EndX=-45.0068 EndY=-123.178 EndZ=0
    g6: LineSegment StartX=-45.0068 StartY=-123.178 StartZ=0 EndX=-94.9992 EndY=-90.0114 EndZ=0
    g7: LineSegment StartX=-94.9992 StartY=-90.0114 StartZ=0 EndX=-94.9992 EndY=-35.0079 EndZ=0
    g8: LineSegment StartX=-94.9992 StartY=-35.0079 StartZ=0 EndX=-59.987 EndY=-35.0079 EndZ=0
    g9: LineSegment StartX=-59.987 StartY=-35.0079 StartZ=0 EndX=-59.987 EndY=34.8273 EndZ=0
    g10: LineSegment StartX=-9.9591 StartY=-91.5603 StartZ=0 EndX=10.0409 EndY=-91.5603 EndZ=0
    g11: LineSegment StartX=10.0409 StartY=-91.5603 StartZ=0 EndX=10.0409 EndY=-95.5603 EndZ=0
    g12: LineSegment StartX=10.0409 StartY=-95.5603 StartZ=0 EndX=-9.9591 EndY=-95.5603 EndZ=0
    g13: LineSegment StartX=-9.9591 StartY=-95.5603 StartZ=0 EndX=-9.9591 EndY=-91.5603 EndZ=0
    g14: Circle CenterX=37.419 CenterY=29.3 CenterZ=0 NormalX=0 NormalY=0 NormalZ=1 AngleXU=0 Radius=1.5
    g15: Circle CenterX=-37.6122 CenterY=29.279 CenterZ=0 NormalX=0 NormalY=0 NormalZ=1 AngleXU=0 Radius=1.5
    g16: Circle CenterX=-0.59146 CenterY=-34.6907 CenterZ=0 NormalX=0 NormalY=0 NormalZ=1 AngleXU=0 Radius=1.5
    g17: Circle CenterX=70.9045 CenterY=-39.7106 CenterZ=0 NormalX=0 NormalY=0 NormalZ=1 AngleXU=0 Radius=1.5
    g18: Circle CenterX=30.5752 CenterY=-118.304 CenterZ=0 NormalX=0 NormalY=0 NormalZ=1 AngleXU=0 Radius=1.5
    g19: Circle CenterX=-31.3681 CenterY=-118.305 CenterZ=0 NormalX=0 NormalY=0 NormalZ=1 AngleXU=0 Radius=1.5
    g20: Circle CenterX=-67.5923 CenterY=-39.7098 CenterZ=0 NormalX=0 NormalY=0 NormalZ=1 AngleXU=0 Radius=1.5
  constraints (35):
    c: Horizontal(g0)
    c: Coincident(g0,g1)
    c: Vertical(g1)
    c: Coincident(g1,g2)
    c: Horizontal(g2)
    c: Coincident(g2,g3)
    c: Vertical(g3)
    c: Coincident(g3,g4)
    c: Coincident(g4,g5)
    c: Horizontal(g5)
    c: Coincident(g5,g6)
    c: Coincident(g6,g7)
    c: Vertical(g7)
    c: Coincident(g7,g8)
    c: Horizontal(g8)
    c: Coincident(g8,g9)
    c: Coincident(g9,g0)
    c: Vertical(g9)
    c: Coincident(g10,g11)
    c: Coincident(g11,g12)
    c: Coincident(g12,g13)
    c: Coincident(g13,g10)
    c: Horizontal(g10)
    c: Horizontal(g12)
    c: Vertical(g11)
    c: Vertical(g13)
    c: Diameter(g14) = 3
    c: Diameter(g15) = 3
    c: Diameter(g16) = 3
    c: Diameter(g17) = 3
    c: Diameter(g18) = 3
    c: Diameter(g19) = 3
    c: Diameter(g20) = 3
    c: DistanceX(g10,g10) = 20
    c: DistanceY(g11,g11) = 4
FEATURE [Part::Extrusion] Extrude026  label="Lid Base"
  Base = -> Sketch025
  Dir = (0,0,1)
  DirMode = 2
  FaceMakerClass = Part::FaceMakerBullseye
  LengthFwd = 3
  LengthRev = 0
  Solid = true
  Symmetric = false
FEATURE [Part::Feature] Part__Feature090  label="Motor Case002"
  shape: bbox 21.76 x 22.71 x 15.75 mm, 88 faces (baked)
FEATURE [Part::Feature] Part__Feature091  label="Case Permanent Magnets"
  Placement = pos=(-1e-15,-3,-1e-15) rot=(0,0,1;3.14159rad)
  shape: bbox 4.402 x 14 x 14.1 mm, 10 faces (baked)
FEATURE [Part::Feature] Part__Feature092  label="Case Permanent Magnets001"
  Placement = pos=(-2e-16,-17,-2e-16) rot=(0,0,1;0rad)
  shape: bbox 4.402 x 14 x 14.1 mm, 10 faces (baked)
FEATURE [Part::Feature] Part__Feature093  label="Front Shaft  Bearing"
  Placement = pos=(0,-20.5,0) rot=(0,1,0;3.21118rad)
  shape: bbox 5.15 x 1.7 x 5.15 mm, 4 faces (baked)
FEATURE [Part::Feature] Part__Feature094  label="Motor Shaft"
  Placement = pos=(2e-15,-30.4,0) rot=(0,1,0;3.21118rad)
  shape: bbox 2 x 38 x 2 mm, 5 faces (baked)
FEATURE [Part::Feature] Part__Feature095  label="Coil Holder"
  Placement = pos=(-2e-15,-17,2e-15) rot=(0,1,0;1.41703rad)
  shape: bbox 12.8 x 12 x 12.8 mm, 43 faces (baked)
FEATURE [Part::Feature] Part__Feature096  label="Coopper Coil"
  Placement = pos=(-2.67174,-5,-1.42602) rot=(0.518237,-0.604744,0.604744;2.18533rad)
  shape: bbox 2.859 x 13 x 3.277 mm, 46 faces (baked)
FEATURE [Part::Feature] Part__Feature097  label="Coopper Coil001"
  Placement = pos=(-1.81064,-17,5.1534) rot=(-0.994118,-0.07658,-0.07658;1.57669rad)
  shape: bbox 3.277 x 13 x 2.859 mm, 46 faces (baked)
FEATURE [Part::Feature] Part__Feature098  label="Coopper Coil002"
  Placement = pos=(-0.54256,-17,-3.02853) rot=(-0.994118,-0.07658,-0.07658;1.57669rad)
  shape: bbox 3.277 x 13 x 2.859 mm, 46 faces (baked)
FEATURE [Part::Feature] Part__Feature099  label="Coopper Coil003"
  Placement = pos=(5.13223,-17,1.80736) rot=(-0.636447,0.545406,0.545406;2.00801rad)
  shape: bbox 2.859 x 13 x 3.277 mm, 46 faces (baked)
FEATURE [Part::Feature] Part__Feature100  label="Motor Cap"
  Placement = pos=(-2e-15,-3,0) rot=(2e-06,0,1;3.14159rad)
  shape: bbox 20.08 x 9.3 x 15.1 mm, 83 faces (baked)
FEATURE [Part::Feature] Part__Feature101  label="Rear Shaft  Bearing"
  Placement = pos=(-7e-15,4.5,1e-15) rot=(0,1,0;1.64038rad)
  shape: bbox 8 x 2 x 8 mm, 6 faces (baked)
FEATURE [Part::Feature] Part__Feature102  label="Collector Spacer"
  Placement = pos=(-5e-15,2.5,4e-15) rot=(0,1,0;1.41703rad)
  shape: bbox 8 x 0.5 x 8 mm, 4 faces (baked)
FEATURE [Part::Feature] Part__Feature103  label="Shaft Collector Support"
  Placement = pos=(-6e-15,1.5,1e-15) rot=(0,1,0;1.41703rad)
  shape: bbox 4 x 3.5 x 4 mm, 4 faces (baked)
FEATURE [Part::Feature] Part__Feature104  label="Shaft Collector"
  Placement = pos=(-5e-15,-3.23245,1e-15) rot=(0,1,0;1.64038rad)
  shape: bbox 5.971 x 3.5 x 5.971 mm, 24 faces, 4 solids (baked)
FEATURE [Part::Feature] Part__Feature105  label="Collector Cap"
  Placement = pos=(-4.25,-1e-15,7.04998) rot=(0,0,1;0rad)
  shape: bbox 8.5 x 3 x 1.9 mm, 20 faces (baked)
FEATURE [Part::Feature] Part__Feature106  label="Collector Blade"
  Placement = pos=(3.4,1,7.79998) rot=(0,0,1;0rad)
  shape: bbox 5.009 x 1 x 10.54 mm, 14 faces (baked)
FEATURE [Part::Feature] Part__Feature107  label="Collector Blade001"
  Placement = pos=(-3.4,1e-15,7.79998) rot=(0,0,1;3.14159rad)
  shape: bbox 5.009 x 1 x 10.54 mm, 14 faces (baked)
FEATURE [App::Part] Asm2  label="Weapon Motor"
  Group = -> [Part__Feature090,Part__Feature091,Part__Feature092,Part__Feature093,Part__Feature094,Part__Feature095,Part__Feature096,Part__Feature097,Part__Feature098,Part__Feature099,Part__Feature100,Part__Feature101,Part__Feature102,Part__Feature103,Part__Feature104,Part__Feature105,Part__Feature106,Part__Feature107]
  Origin = -> Origin007
  Placement = pos=(-18.25,-110.5,45.5) rot=(0,0,-1;4.71239rad)
FEATURE [Part::Fillet] Fillet
  Base = -> Extrude026
  Edges = 21 edges r=1: [Edge4,Edge7,Edge10,Edge13,Edge16,Edge19,Edge22,Edge25,Edge28,Edge30,Edge34,Edge37,Edge40,Edge42,Edge45,Edge48,Edge51,Edge54,Edge57,Edge60,Edge63]
FEATURE [Sketcher::SketchObject] Sketch026
  FullyConstrained = true
  MapMode = 5
  Placement = pos=(0,0,38) rot=(0,0,1;0rad)
  Support = -> [Fillet]
  sketch-geometry (1):
    g0: Circle CenterX=0 CenterY=-110 CenterZ=0 NormalX=0 NormalY=0 NormalZ=1 AngleXU=0 Radius=2
  constraints (3):
    c: Diameter(g0) = 4
    c: DistanceY(g0,g-1) = 110
    c: PointOnObject(g0,g-2)
FEATURE [Part::Extrusion] Extrude027  label="Weapon Wire slot"
  Base = -> Sketch026
  Dir = (0,0,1)
  DirMode = 2
  FaceMakerClass = Part::FaceMakerBullseye
  LengthFwd = 10
  LengthRev = 0
  Placement = pos=(-27,0,-6.5) rot=(0,0,1;0rad)
  Solid = true
  Symmetric = false
FEATURE [Part::Cut] Cut007
  Base = -> Fillet
  Refine = true
  Tool = -> Extrude027
FEATURE [Sketcher::SketchObject] Sketch028
  FullyConstrained = true
  MapMode = 5
  Placement = pos=(0,0,38) rot=(0,0,1;0rad)
  Support = -> [Cut007]
  sketch-geometry (9):
    g0: LineSegment StartX=-17 StartY=-100 StartZ=0 EndX=0 EndY=-100 EndZ=0
    g1: LineSegment StartX=0 StartY=-100 StartZ=0 EndX=0 EndY=-102 EndZ=0
    g2: LineSegment StartX=0 StartY=-102 StartZ=0 EndX=-17 EndY=-102 EndZ=0
    g3: LineSegment StartX=-17 StartY=-102 StartZ=0 EndX=-17 EndY=-100 EndZ=0
    g4: LineSegment StartX=-17 StartY=-118 StartZ=0 EndX=0 EndY=-118 EndZ=0
    g5: LineSegment StartX=0 StartY=-118 StartZ=0 EndX=0 EndY=-120 EndZ=0
    g6: LineSegment StartX=0 StartY=-120 StartZ=0 EndX=-17 EndY=-120 EndZ=0
    g7: LineSegment StartX=-17 StartY=-120 StartZ=0 EndX=-17 EndY=-118 EndZ=0
    g8: LineSegment StartX=0 StartY=-102 StartZ=0 EndX=0 EndY=-118 EndZ=0
  constraints (26):
    c: Coincident(g0,g1)
    c: Coincident(g1,g2)
    c: Coincident(g2,g3)
    c: Coincident(g3,g0)
    c: Horizontal(g2)
    c: Vertical(g1)
    c: Vertical(g3)
    c: Coincident(g4,g5)
    c: Coincident(g5,g6)
    c: Coincident(g6,g7)
    c: Coincident(g7,g4)
    c: Horizontal(g4)
    c: Horizontal(g6)
    c: Vertical(g5)
    c: Vertical(g7)
    c: Distance(g1,g4) = 16
    c: Distance(g-1,g0) = 100
    c: DistanceX(g0,g0) = 17
    c: DistanceY(g3,g3) = 2
    c: DistanceY(g5,g5) = 2
    c: DistanceX(g6,g6) = 17
    c: Coincident(g8,g1)
    c: Coincident(g8,g4)
    c: Vertical(g8)
    c: DistanceY(g1,g1) = 2
    c: PointOnObject(g0,g-2)
FEATURE [Part::Extrusion] Extrude028  label="Motor Flange Gap"
  Base = -> Sketch028
  Dir = (0,0,1)
  DirMode = 2
  FaceMakerClass = Part::FaceMakerBullseye
  LengthFwd = 10
  LengthRev = 0
  Solid = true
  Symmetric = true
FEATURE [Part::Cut] Cut008
  Base = -> Cut007
  Refine = true
  Tool = -> Extrude028
FEATURE [Sketcher::SketchObject] Sketch030
  FullyConstrained = false
  Placement = pos=(0,0,0) rot=(0.57735,0.57735,0.57735;2.0944rad)
  sketch-geometry (5):
    g0: LineSegment StartX=0 StartY=45.51 StartZ=0 EndX=-34.7613 EndY=45.51 EndZ=0
    g1: Circle CenterX=-18.5 CenterY=45.51 CenterZ=0 NormalX=0 NormalY=0 NormalZ=1 AngleXU=0 Radius=1.1
    g2: Circle CenterX=-18.5 CenterY=45.51 CenterZ=0 NormalX=0 NormalY=0 NormalZ=1 AngleXU=0 Radius=7.5
    g3: LineSegment StartX=-18.5 StartY=45.51 StartZ=0 EndX=-18.5 EndY=53.8942 EndZ=0
    g4: LineSegment StartX=-18.5 StartY=45.51 StartZ=0 EndX=-18.5 EndY=38.7803 EndZ=0
  constraints (12):
    c: PointOnObject(g0,g-2)
    c: Horizontal(g0)
    c: DistanceY(g-1,g0) = 45.51
    c: PointOnObject(g1,g0)
    c: Diameter(g1) = 2.2
    c: Coincident(g2,g1)
    c: Diameter(g2) = 15
    c: Coincident(g3,g1)
    c: Vertical(g3)
    c: Coincident(g4,g1)
    c: Vertical(g4)
    c: DistanceX(g-2,g1) = -18.5
FEATURE [Sketcher::SketchObject] Sketch031
  FullyConstrained = true
  MapMode = 5
  Placement = pos=(6,0,0) rot=(0.57735,0.57735,0.57735;2.0944rad)
  sketch-geometry (2):
    g0: Circle CenterX=-18.5 CenterY=45.51 CenterZ=0 NormalX=0 NormalY=0 NormalZ=1 AngleXU=0 Radius=10
    g1: Circle CenterX=-18.5 CenterY=45.51 CenterZ=0 NormalX=0 NormalY=0 NormalZ=1 AngleXU=0 Radius=6
  constraints (5):
    c: DistanceX(g-2,g0) = -18.5
    c: DistanceY(g-1,g0) = 45.51
    c: Coincident(g1,g0)
    c: Diameter(g0) = 20
    c: Diameter(g1) = 12
FEATURE [Sketcher::SketchObject] Sketch032
  FullyConstrained = false
  MapMode = 5
  Placement = pos=(0,0,38) rot=(0,0,1;0rad)
  Support = -> [Cut008]
  sketch-geometry (8):
    g0: Circle CenterX=-20 CenterY=0 CenterZ=0 NormalX=0 NormalY=0 NormalZ=1 AngleXU=0 Radius=2
    g1: ArcOfCircle CenterX=-20 CenterY=0 CenterZ=0 NormalX=0 NormalY=0 NormalZ=1 AngleXU=0 Radius=5.84308 StartAngle=1.5708 EndAngle=4.71239
    g2: LineSegment StartX=-20 StartY=5.84308 StartZ=0 EndX=0 EndY=5.84308 EndZ=0
    g3: LineSegment StartX=-20 StartY=-5.84308 StartZ=0 EndX=0 EndY=-5.84308 EndZ=0
    g4: Circle CenterX=20 CenterY=0 CenterZ=0 NormalX=0 NormalY=0 NormalZ=1 AngleXU=0 Radius=2
    g5: ArcOfCircle CenterX=20 CenterY=0 CenterZ=0 NormalX=0 NormalY=0 NormalZ=1 AngleXU=0 Radius=5.84308 StartAngle=4.71239 EndAngle=7.85398
    g6: LineSegment StartX=20 StartY=5.84308 StartZ=0 EndX=0 EndY=5.84308 EndZ=0
    g7: LineSegment StartX=20 StartY=-5.84308 StartZ=0 EndX=0 EndY=-5.84308 EndZ=0
  constraints (15):
    c: PointOnObject(g0,g-1)
    c: Diameter(g0) = 4
    c: DistanceX(g0,g-1) = 20
    c: Coincident(g1,g0)
    c: PointOnObject(g2,g-2)
    c: Horizontal(g2)
    c: Horizontal(g3)
    c: Tangent(g1,g3) = -1.5708
    c: Tangent(g1,g2) = 1.5708
    c: Diameter(g4) = 4
    c: Coincident(g5,g4)
    c: Horizontal(g6)
    c: Horizontal(g7)
    c: Tangent(g5,g7) = 1.5708
    c: Tangent(g5,g6) = -1.5708
FEATURE [Part::Extrusion] Extrude031  label="Weapon Base"
  Base = -> Sketch032
  Dir = (0,0,1)
  DirMode = 2
  FaceMakerClass = Part::FaceMakerBullseye
  LengthFwd = 3
  LengthRev = 0
  Solid = true
  Symmetric = false
FEATURE [Sketcher::SketchObject] Sketch033
  FullyConstrained = false
  MapMode = 5
  Placement = pos=(0,0,41) rot=(0,0,1;0rad)
  Support = -> [Extrude031]
  sketch-geometry (2):
    g0: Circle CenterX=19.9922 CenterY=0 CenterZ=0 NormalX=0 NormalY=0 NormalZ=1 AngleXU=0 Radius=2
    g1: Circle CenterX=-19.9922 CenterY=0 CenterZ=0 NormalX=0 NormalY=0 NormalZ=1 AngleXU=0 Radius=2
  constraints (3):
    c: PointOnObject(g0,g-1)
    c: Diameter(g0) = 4
    c: Diameter(g1) = 4
FEATURE [Part::Extrusion] Extrude032  label="Lid Weapon Holes"
  Base = -> Sketch033
  Dir = (0,0,1)
  DirMode = 2
  FaceMakerClass = Part::FaceMakerBullseye
  LengthFwd = 10
  LengthRev = 0
  Solid = true
  Symmetric = true
FEATURE [Part::Cut] Cut010  label="Robot Lid"
  Base = -> Cut008
  Refine = true
  Tool = -> Extrude032
FEATURE [Sketcher::SketchObject] Sketch034
  FullyConstrained = false
  Placement = pos=(0,0,0) rot=(0.57735,0.57735,0.57735;2.0944rad)
  sketch-geometry (9):
    g0: LineSegment StartX=-5.83 StartY=45.92 StartZ=0 EndX=-5.83 EndY=40.92 EndZ=0
    g1: LineSegment StartX=-5.83 StartY=40.92 StartZ=0 EndX=5.83 EndY=40.92 EndZ=0
    g2: LineSegment StartX=5.83 StartY=40.92 StartZ=0 EndX=5.83 EndY=45.92 EndZ=0
    g3: ArcOfCircle CenterX=-25.7931 CenterY=39.7062 CenterZ=0 NormalX=0 NormalY=0 NormalZ=1 AngleXU=0 Radius=20.9078 StartAngle=0.301757 EndAngle=1.49015
    g4: ArcOfCircle CenterX=-25.7931 CenterY=39.7062 CenterZ=0 NormalX=0 NormalY=0 NormalZ=1 AngleXU=0 Radius=32.2278 StartAngle=0.194023 EndAngle=1.49015
    g5: LineSegment StartX=-23.1969 StartY=71.8293 StartZ=0 EndX=-151.498 EndY=82.1987 EndZ=0
    g6: LineSegment StartX=-24.1088 StartY=60.5461 StartZ=0 EndX=-151.69 EndY=70.8573 EndZ=0
    g7: ArcOfCircle CenterX=-143.144 CenterY=76.3844 CenterZ=0 NormalX=0 NormalY=0 NormalZ=1 AngleXU=0 Radius=10.1777 StartAngle=2.53354 EndAngle=3.71567
    g8: Circle CenterX=-143.144 CenterY=76.3844 CenterZ=0 NormalX=0 NormalY=0 NormalZ=1 AngleXU=0 Radius=1.9
  constraints (21):
    c: Coincident(g0,g1)
    c: Coincident(g1,g2)
    c: Horizontal(g1)
    c: Vertical(g0)
    c: Vertical(g2)
    c: Symmetric(g2,g0,g-2)
    c: DistanceY(g0,g0) = 5
    c: Coincident(g3,g0)
    c: Coincident(g4,g3)
    c: Coincident(g4,g2)
    c: DistanceX(g1,g1) = 11.66
    c: Distance(g3,g0) = 20
    c: Distance(g1,g-1) = 40.92
    c: Parallel(g5,g6)
    c: Tangent(g6,g3) = -1.5708
    c: Tangent(g5,g4) = -1.5708
    c: Distance(g3,g4) = 11.32
    c: Coincident(g7,g5)
    c: Coincident(g7,g6)
    c: Coincident(g8,g7)
    c: Diameter(g8) = 3.8
FEATURE [Part::Extrusion] Extrude033  label="Weapon Sling"
  Base = -> Sketch034
  Dir = (1,0,0)
  DirMode = 2
  FaceMakerClass = Part::FaceMakerBullseye
  LengthFwd = 3
  LengthRev = 0
  Solid = true
  Symmetric = true
FEATURE [Part::MultiFuse] Fusion016  label="Weapon Holder"
  Refine = true
  Shapes = -> [Extrude031,Extrude033]
FEATURE [Sketcher::SketchObject] Sketch037
  FullyConstrained = false
  MapMode = 5
  Placement = pos=(-1.5,0,0) rot=(0.57735,-0.57735,-0.57735;2.0944rad)
  Support = -> [Fusion016]
  sketch-geometry (1):
    g0: Circle CenterX=54.8268 CenterY=76.655 CenterZ=0 NormalX=0 NormalY=0 NormalZ=1 AngleXU=0 Radius=1.85
  constraints (1):
    c: Diameter(g0) = 3.7
FEATURE [Part::Extrusion] Extrude036  label="Cilinder Gear"
  Base = -> Sketch037
  Dir = (-1,0,0)
  DirMode = 2
  FaceMakerClass = Part::FaceMakerBullseye
  LengthFwd = 20
  LengthRev = 0
  Placement = pos=(12.3,-93,0) rot=(0,0,1;0rad)
  Solid = true
  Symmetric = false
FEATURE [Sketcher::SketchObject] Sketch039
  FullyConstrained = false
  MapMode = 5
  Placement = pos=(-2,-93,0) rot=(0.57735,-0.57735,-0.57735;2.0944rad)
  sketch-geometry (1):
    g0: Circle CenterX=54.7831 CenterY=76.6691 CenterZ=0 NormalX=0 NormalY=0 NormalZ=1 AngleXU=0 Radius=4
  constraints (1):
    c: Diameter(g0) = 8
FEATURE [Part::Extrusion] Extrude037  label="Kunai Drive Stopper"
  Base = -> Sketch039
  Dir = (-1,0,0)
  DirMode = 2
  FaceMakerClass = Part::FaceMakerBullseye
  LengthFwd = 3
  LengthRev = 0
  Solid = true
  Symmetric = false
FEATURE [Mesh::Feature] Kunai
  Placement = pos=(5.3,-148.1,60.7) rot=(0,1,0;4.71239rad)
FEATURE [Sketcher::SketchObject] Sketch040
  FullyConstrained = false
  Placement = pos=(0,0,0) rot=(0.57735,0.57735,0.57735;2.0944rad)
  sketch-geometry (8):
    g0: ArcOfCircle CenterX=-54.7336 CenterY=76.5245 CenterZ=0 NormalX=0 NormalY=0 NormalZ=1 AngleXU=0 Radius=5 StartAngle=0.86388 EndAngle=4.00547
    g1: ArcOfCircle CenterX=-18.2895 CenterY=45.3946 CenterZ=0 NormalX=0 NormalY=0 NormalZ=1 AngleXU=0 Radius=5 StartAngle=4.00547 EndAngle=7.14707
    g2: LineSegment StartX=-51.4861 StartY=80.3264 StartZ=0 EndX=-15.042 EndY=49.1965 EndZ=0
    g3: LineSegment StartX=-57.9811 StartY=72.7227 StartZ=0 EndX=-21.5369 EndY=41.5928 EndZ=0
    g4: ArcOfCircle CenterX=-54.7336 CenterY=76.5245 CenterZ=0 NormalX=0 NormalY=0 NormalZ=1 AngleXU=0 Radius=6 StartAngle=0.86388 EndAngle=4.00547
    g5: ArcOfCircle CenterX=-18.2895 CenterY=45.3946 CenterZ=0 NormalX=0 NormalY=0 NormalZ=1 AngleXU=0 Radius=6 StartAngle=4.00547 EndAngle=7.14707
    g6: LineSegment StartX=-50.8366 StartY=81.0867 StartZ=0 EndX=-14.3925 EndY=49.9568 EndZ=0
    g7: LineSegment StartX=-58.6305 StartY=71.9623 StartZ=0 EndX=-22.1864 EndY=40.8324 EndZ=0
  constraints (16):
    c: Diameter(g1) = 10
    c: Diameter(g0) = 10
    c: Equal(g3,g2)
    c: Tangent(g0,g2) = 1.5708
    c: Coincident(g1,g2)
    c: Tangent(g1,g3) = -1.5708
    c: Coincident(g4,g0)
    c: Coincident(g5,g1)
    c: Diameter(g4) = 12
    c: Diameter(g5) = 12
    c: Tangent(g5,g7) = -1.5708
    c: Tangent(g5,g6) = 1.5708
    c: PointOnObject(g4,g7)
    c: Tangent(g7,g4) = -1.5708
    c: Tangent(g4,g6) = 1.5708
    c: Tangent(g0,g3) = -1.5708
FEATURE [Part::Extrusion] Extrude038  label="Rubber Band"
  Base = -> Sketch040
  Dir = (1,0,0)
  DirMode = 2
  FaceMakerClass = Part::FaceMakerBullseye
  LengthFwd = 2
  LengthRev = 0
  Placement = pos=(7,-93,0) rot=(0,0,1;0rad)
  Solid = true
  Symmetric = false
FEATURE [Part::Extrusion] Extrude039
  Base = -> Sketch030
  Dir = (1,0,0)
  DirMode = 2
  FaceMakerClass = Part::FaceMakerBullseye
  LengthFwd = 6
  LengthRev = 0
  Solid = true
  Symmetric = false
FEATURE [Part::Extrusion] Extrude040
  Base = -> Sketch031
  Dir = (1,0,0)
  DirMode = 2
  FaceMakerClass = Part::FaceMakerBullseye
  LengthFwd = 3
  LengthRev = 0
  Placement = pos=(-4.5,0,0) rot=(0,0,1;0rad)
  Solid = true
  Symmetric = false
FEATURE [Part::Cut] Cut011  label="Motor Band Gear"
  Base = -> Extrude039
  Placement = pos=(5,-92,0) rot=(0,0,1;0rad)
  Refine = true
  Tool = -> Extrude040
FEATURE [Part::Feature] Part__Feature108  label="Motor Band Gear001"
  Placement = pos=(5,-129.5,31) rot=(0,0,1;0rad)
  shape: bbox 6 x 15 x 15 mm, 8 faces (baked)
FEATURE [Part::Extrusion] Extrude041  label="Cilinder Gear001"
  Base = -> Sketch037
  Dir = (-1,0,0)
  DirMode = 2
  FaceMakerClass = Part::FaceMakerBullseye
  LengthFwd = 15
  LengthRev = 0
  Placement = pos=(12.3,-93,0) rot=(0,0,1;0rad)
  Solid = true
  Symmetric = false
FEATURE [Part::Cut] Cut012  label="Stopper"
  Base = -> Extrude037
  Refine = true
  Tool = -> Extrude041
FEATURE [Part::MultiFuse] Fusion017  label="Kunai Chain gear"
  Placement = pos=(0,0,-0.5) rot=(0,0,1;0rad)
  Refine = true
  Shapes = -> [Part__Feature108,Extrude036]
FEATURE [Part::Feature] Part__Feature109  label="Robot Rim"
  shape: bbox 40 x 40 x 20.01 mm, 43 faces (baked)
FEATURE [Part::Feature] Part__Feature110  label="Robot Tire"
  shape: bbox 49.79 x 49.79 x 19 mm, 10 faces (baked)
FEATURE [App::Part] TIRE  label="Left Tire"
  Group = -> [Part__Feature109,Part__Feature110]
  Origin = -> Origin008
  Placement = pos=(-60.5,0,6.5) rot=(0,1,0;4.71239rad)
FEATURE [Part::Feature] Part__Feature111  label="Robot Rim001"
  shape: bbox 40 x 40 x 20.01 mm, 43 faces (baked)
FEATURE [Part::Feature] Part__Feature112  label="Robot Tire001"
  shape: bbox 49.79 x 49.79 x 19 mm, 10 faces (baked)
FEATURE [App::Part] TIRE001  label="Right Tire"
  Group = -> [Part__Feature111,Part__Feature112]
  Origin = -> Origin009
  Placement = pos=(60.5,2.4e-15,6.5) rot=(-0.707107,0,-0.707107;3.14159rad)
FEATURE [Sketcher::SketchObject] Sketch042
  FullyConstrained = false
  MapMode = 5
  Placement = pos=(0,0,41) rot=(0,0,1;0rad)
  Support = -> [Fusion016]
  sketch-geometry (8):
    g0: LineSegment StartX=1.5 StartY=5.875 StartZ=0 EndX=16.9097 EndY=5.875 EndZ=0
    g1: LineSegment StartX=16.9097 StartY=5.875 StartZ=0 EndX=16.9097 EndY=-5.875 EndZ=0
    g2: LineSegment StartX=16.9097 StartY=-5.875 StartZ=0 EndX=1.5 EndY=-5.875 EndZ=0
    g3: LineSegment StartX=1.5 StartY=-5.875 StartZ=0 EndX=1.5 EndY=5.875 EndZ=0
    g4: LineSegment StartX=-1.5 StartY=5.875 StartZ=0 EndX=-16.9097 EndY=5.875 EndZ=0
    g5: LineSegment StartX=-16.9097 StartY=5.875 StartZ=0 EndX=-16.9097 EndY=-5.875 EndZ=0
    g6: LineSegment StartX=-16.9097 StartY=-5.875 StartZ=0 EndX=-1.5 EndY=-5.875 EndZ=0
    g7: LineSegment StartX=-1.5 StartY=-5.875 StartZ=0 EndX=-1.5 EndY=5.875 EndZ=0
  constraints (19):
    c: Coincident(g0,g1)
    c: Coincident(g1,g2)
    c: Coincident(g2,g3)
    c: Coincident(g3,g0)
    c: Horizontal(g0)
    c: Horizontal(g2)
    c: Vertical(g1)
    c: Vertical(g3)
    c: DistanceY(g1,g1) = 11.75
    c: DistanceY(g-1,g0) = 5.875
    c: DistanceX(g-2,g0) = 1.5
    c: Coincident(g4,g5)
    c: Coincident(g5,g6)
    c: Coincident(g6,g7)
    c: Coincident(g7,g4)
    c: Horizontal(g4)
    c: Horizontal(g6)
    c: Vertical(g5)
    c: Vertical(g7)
FEATURE [Part::Extrusion] Extrude042
  Base = -> Sketch042
  Dir = (0,0,1)
  DirMode = 2
  FaceMakerClass = Part::FaceMakerBullseye
  LengthFwd = 5
  LengthRev = 0
  Solid = true
  Symmetric = false
FEATURE [Sketcher::SketchObject] Sketch043
  FullyConstrained = false
  MapMode = 45
  Placement = pos=(0,-5.875,43.5) rot=(0.57735,0.57735,0.57735;4.18879rad)
  Support = -> [Extrude042]
  sketch-geometry (4):
    g0: LineSegment StartX=3.07193 StartY=-17.6179 StartZ=0 EndX=-1.78812 EndY=-17.6179 EndZ=0
    g1: LineSegment StartX=-1.78812 StartY=-17.6179 StartZ=0 EndX=-1.78812 EndY=-16.8506 EndZ=0
    g2: LineSegment StartX=-1.78812 StartY=-16.8506 StartZ=0 EndX=3.07193 EndY=0 EndZ=0
    g3: LineSegment StartX=3.07193 StartY=0 StartZ=0 EndX=3.07193 EndY=-17.6179 EndZ=0
  constraints (7):
    c: Horizontal(g0)
    c: Coincident(g0,g1)
    c: Vertical(g1)
    c: Coincident(g1,g2)
    c: Coincident(g2,g3)
    c: Vertical(g3)
    c: Coincident(g0,g3)
FEATURE [Part::Extrusion] Extrude043
  Base = -> Sketch043
  Dir = (0,1,0)
  DirMode = 2
  FaceMakerClass = Part::FaceMakerBullseye
  LengthFwd = 100
  LengthRev = 100
  Solid = true
  Symmetric = false
FEATURE [Part::Extrusion] Extrude044
  Base = -> Sketch043
  Dir = (0,1,0)
  DirMode = 2
  FaceMakerClass = Part::FaceMakerBullseye
  LengthFwd = 100
  LengthRev = 100
  Placement = pos=(0,0,0) rot=(0,0,1;3.14159rad)
  Solid = true
  Symmetric = false
FEATURE [Part::MultiFuse] Fusion018  label="Reinforcements Cut"
  Refine = true
  Shapes = -> [Extrude044,Extrude043]
FEATURE [Part::Cut] Cut013  label="Weapon Holder Reinforcement"
  Base = -> Extrude042
  Refine = true
  Tool = -> Fusion018
FEATURE [Part::MultiFuse] Fusion019  label="Weapon Holder001"
  Refine = true
  Shapes = -> [Fusion016,Cut013]
FEATURE [Sketcher::SketchObject] Sketch044
  FullyConstrained = false
  MapMode = 5
  Placement = pos=(-5,0,0) rot=(0.57735,-0.57735,-0.57735;2.0944rad)
  Support = -> [Cut012]
  sketch-geometry (1):
    g0: Circle CenterX=147.795 CenterY=76.6448 CenterZ=0 NormalX=0 NormalY=0 NormalZ=1 AngleXU=0 Radius=1.9
  constraints (1):
    c: Diameter(g0) = 3.8
FEATURE [Part::Extrusion] Extrude045
  Base = -> Sketch044
  Dir = (-1,0,0)
  DirMode = 2
  FaceMakerClass = Part::FaceMakerBullseye
  LengthFwd = 10
  LengthRev = 0
  Solid = true
  Symmetric = true
FEATURE [Sketcher::SketchObject] Sketch045
  FullyConstrained = false
  MapMode = 5
  Placement = pos=(0,0,38) rot=(0,0,1;0rad)
  Support = -> [Cut010]
  sketch-geometry (6):
    g0: LineSegment StartX=-15 StartY=-57.3216 StartZ=0 EndX=15 EndY=-57.3216 EndZ=0
    g1: LineSegment StartX=15 StartY=-67.3216 StartZ=0 EndX=-15 EndY=-67.3216 EndZ=0
    g2: Circle CenterX=12 CenterY=-62.3216 CenterZ=0 NormalX=0 NormalY=0 NormalZ=1 AngleXU=0 Radius=2
    g3: ArcOfCircle CenterX=12 CenterY=-62.3216 CenterZ=0 NormalX=0 NormalY=0 NormalZ=1 AngleXU=0 Radius=5.83095 StartAngle=5.25281 EndAngle=7.31356
    g4: Circle CenterX=-12 CenterY=-62.3216 CenterZ=0 NormalX=0 NormalY=0 NormalZ=1 AngleXU=0 Radius=2
    g5: ArcOfCircle CenterX=-12 CenterY=-62.3216 CenterZ=0 NormalX=0 NormalY=0 NormalZ=1 AngleXU=0 Radius=5.83095 StartAngle=2.11122 EndAngle=4.17197
  constraints (13):
    c: Horizontal(g0)
    c: Horizontal(g1)
    c: DistanceY(g1,g0) = 10
    c: DistanceX(g0,g0) = 30
    c: DistanceX(g-2,g0) = 15
    c: Diameter(g2) = 4
    c: Distance(g2,g0) = 5
    c: DistanceX(g-2,g2) = 12
    c: Coincident(g3,g2)
    c: Coincident(g3,g0)
    c: Coincident(g3,g1)
    c: Diameter(g4) = 4
    c: Coincident(g5,g4)
FEATURE [Part::Extrusion] Extrude046  label="MIddle Base"
  Base = -> Sketch045
  Dir = (0,0,1)
  DirMode = 2
  FaceMakerClass = Part::FaceMakerBullseye
  LengthFwd = 3
  LengthRev = 0
  Solid = true
  Symmetric = false
FEATURE [Sketcher::SketchObject] Sketch046
  FullyConstrained = false
  MapMode = 5
  Placement = pos=(0,0,41) rot=(0,0,1;0rad)
  Support = -> [Extrude046]
  sketch-geometry (4):
    g0: LineSegment StartX=-1.49987 StartY=-57.3217 StartZ=0 EndX=1.50013 EndY=-57.3217 EndZ=0
    g1: LineSegment StartX=1.50013 StartY=-57.3217 StartZ=0 EndX=1.50013 EndY=-67.3217 EndZ=0
    g2: LineSegment StartX=1.50013 StartY=-67.3217 StartZ=0 EndX=-1.49987 EndY=-67.3217 EndZ=0
    g3: LineSegment StartX=-1.49987 StartY=-67.3217 StartZ=0 EndX=-1.49987 EndY=-57.3217 EndZ=0
  constraints (10):
    c: Coincident(g0,g1)
    c: Coincident(g1,g2)
    c: Coincident(g2,g3)
    c: Coincident(g3,g0)
    c: Horizontal(g0)
    c: Horizontal(g2)
    c: Vertical(g1)
    c: Vertical(g3)
    c: DistanceY(g1,g1) = 10
    c: DistanceX(g0,g0) = 3
FEATURE [Part::Extrusion] Extrude047  label="Middle Holder"
  Base = -> Sketch046
  Dir = (0,0,1)
  DirMode = 2
  FaceMakerClass = Part::FaceMakerBullseye
  LengthFwd = 25
  LengthRev = 0
  Solid = true
  Symmetric = false
FEATURE [Part::MultiFuse] Fusion020  label="MIddle Support"
  Refine = true
  Shapes = -> [Extrude046,Extrude047]
FEATURE [Part::MultiFuse] Fusion021  label="Weapon Holder With Supports"
  Refine = true
  Shapes = -> [Fusion020,Fusion019]
FEATURE [Sketcher::SketchObject] Sketch047
  FullyConstrained = false
  MapMode = 5
  Placement = pos=(0,0,38) rot=(0,0,1;0rad)
  Support = -> [Cut010]
  sketch-geometry (2):
    g0: Circle CenterX=12.0091 CenterY=-62.3033 CenterZ=0 NormalX=0 NormalY=0 NormalZ=1 AngleXU=0 Radius=2
    g1: Circle CenterX=-12.0091 CenterY=-62.3033 CenterZ=0 NormalX=0 NormalY=0 NormalZ=1 AngleXU=0 Radius=2
  constraints (2):
    c: Diameter(g0) = 4
    c: Diameter(g1) = 4
FEATURE [Part::Extrusion] Extrude048  label="Middle Holder Screw Holes"
  Base = -> Sketch047
  Dir = (0,0,1)
  DirMode = 2
  FaceMakerClass = Part::FaceMakerBullseye
  LengthFwd = 10
  LengthRev = 0
  Solid = true
  Symmetric = true
FEATURE [Part::Cut] Cut015  label="Lid With Holes"
  Base = -> Cut010
  Refine = true
  Tool = -> Extrude048
FEATURE [Sketcher::SketchObject] Sketch049
  FullyConstrained = false
  MapMode = 5
  Placement = pos=(11,0,-0.5) rot=(0.57735,0.57735,0.57735;2.0944rad)
  Support = -> [Fusion017]
  sketch-geometry (2):
    g0: Circle CenterX=-148.033 CenterY=76.5072 CenterZ=0 NormalX=0 NormalY=0 NormalZ=1 AngleXU=0 Radius=7.25
    g1: Circle CenterX=-148.033 CenterY=76.5072 CenterZ=0 NormalX=0 NormalY=0 NormalZ=1 AngleXU=0 Radius=10
  constraints (3):
    c: Diameter(g0) = 14.5
    c: Coincident(g1,g0)
    c: Diameter(g1) = 20
FEATURE [Part::Extrusion] Extrude049  label="Band Reinforcement"
  Base = -> Sketch049
  Dir = (1,0,0)
  DirMode = 2
  FaceMakerClass = Part::FaceMakerBullseye
  LengthFwd = -1.5
  LengthRev = 0
  Solid = true
  Symmetric = false
FEATURE [Part::Extrusion] Extrude050  label="Band Reinforcement001"
  Base = -> Sketch049
  Dir = (1,0,0)
  DirMode = 2
  FaceMakerClass = Part::FaceMakerBullseye
  LengthFwd = -1.5
  LengthRev = 0
  Placement = pos=(-4.5,0,0) rot=(0,0,1;0rad)
  Solid = true
  Symmetric = false
FEATURE [Part::Extrusion] Extrude051  label="Band Reinforcement002"
  Base = -> Sketch049
  Dir = (1,0,0)
  DirMode = 2
  FaceMakerClass = Part::FaceMakerBullseye
  LengthFwd = -1.5
  LengthRev = 0
  Placement = pos=(0,37.5,-30.5) rot=(0,0,1;0rad)
  Solid = true
  Symmetric = false
FEATURE [Part::MultiFuse] Fusion022  label="Top Reinforcement"
  Refine = true
  Shapes = -> [Extrude049,Extrude050]
FEATURE [Part::MultiFuse] Fusion023  label="Kunai Gear"
  Refine = true
  Shapes = -> [Fusion017,Fusion022]
FEATURE [Part::Extrusion] Extrude052  label="Band Reinforcement003"
  Base = -> Sketch049
  Dir = (1,0,0)
  DirMode = 2
  FaceMakerClass = Part::FaceMakerBullseye
  LengthFwd = -1.5
  LengthRev = 0
  Placement = pos=(-4.5,37.5,-30.5) rot=(0,0,1;0rad)
  Solid = true
  Symmetric = false
FEATURE [Part::MultiFuse] Fusion024  label="Bottom Reinforcement"
  Refine = true
  Shapes = -> [Extrude052,Extrude051]
FEATURE [Part::MultiFuse] Fusion025  label="Motor Reinforced Gear"
  Refine = true
  Shapes = -> [Cut011,Fusion024]
FEATURE [Sketcher::SketchObject] Sketch050
  FullyConstrained = false
  MapMode = 5
  Placement = pos=(0,0,38) rot=(0,0,1;0rad)
  Support = -> [Cut015]
  sketch-geometry (4):
    g0: LineSegment StartX=3.04477 StartY=-98.7376 StartZ=0 EndX=13.0448 EndY=-98.7376 EndZ=0
    g1: LineSegment StartX=13.0448 StartY=-98.7376 StartZ=0 EndX=13.0448 EndY=-121.738 EndZ=0
    g2: LineSegment StartX=13.0448 StartY=-121.738 StartZ=0 EndX=3.04477 EndY=-121.738 EndZ=0
    g3: LineSegment StartX=3.04477 StartY=-121.738 StartZ=0 EndX=3.04477 EndY=-98.7376 EndZ=0
  constraints (10):
    c: Coincident(g0,g1)
    c: Coincident(g1,g2)
    c: Coincident(g2,g3)
    c: Coincident(g3,g0)
    c: Horizontal(g0)
    c: Horizontal(g2)
    c: Vertical(g1)
    c: Vertical(g3)
    c: DistanceX(g0,g0) = 10
    c: DistanceY(g1,g1) = 23
FEATURE [Part::Extrusion] Extrude053  label="Motor Gear Lid Gap"
  Base = -> Sketch050
  Dir = (0,0,1)
  DirMode = 2
  FaceMakerClass = Part::FaceMakerBullseye
  LengthFwd = 7
  LengthRev = 0
  Solid = true
  Symmetric = true
FEATURE [Part::Cut] Cut016  label="Lid"
  Base = -> Cut015
  Refine = true
  Tool = -> Extrude053
FEATURE [Part::Feature] Part__Feature113  label="PCB MX1508"
  shape: bbox 24.5 x 1.62 x 21.2 mm, 502 faces (baked)
FEATURE [Part::Feature] Part__Feature114  label="smd100uF16VRVT"
  Placement = pos=(3.4012,1.65,-5.66553) rot=(0,-1,0;1.57952rad)
  shape: bbox 8.064 x 5.76 x 9.017 mm, 161 faces, 6 solids (baked)
FEATURE [Part::Feature] Part__Feature115  label="smd100uF16VRVT001"
  Placement = pos=(-3.69416,1.65,-5.66553) rot=(0,1,0;1.55334rad)
  shape: bbox 8.063 x 5.76 x 9.034 mm, 161 faces, 6 solids (baked)
FEATURE [Part::Feature] Part__Feature116  label="smdChip16pin"
  Placement = pos=(0.38974,1.52498,9.68189) rot=(0,1,0;3.14159rad)
  shape: bbox 7.3 x 1.227 x 10 mm, 477 faces, 17 solids (baked)
FEATURE [Part::Feature] Part__Feature117  label="smdResistor2200"
  Placement = pos=(10.7501,0.8,-6.22873) rot=(0,1,0;1.5708rad)
  shape: bbox 1.307 x 0.6262 x 2.511 mm, 79 faces, 3 solids (baked)
FEATURE [Part::Feature] Part__Feature118  label="smdDiode"
  Placement = pos=(8.50324,1.45,-6.59956) rot=(0,1,0;1.5708rad)
  shape: bbox 1.407 x 1.407 x 3.85 mm, 60 faces (baked)
FEATURE [App::Part] MX1508
  Group = -> [Part__Feature113,Part__Feature114,Part__Feature115,Part__Feature116,Part__Feature117,Part__Feature118]
  Origin = -> Origin010
  Placement = pos=(0,8,5.5) rot=(1,0,0;1.5708rad)
FEATURE [Part::Cut] Cut014  label="Gear Stopper"
  Base = -> Cut012
  Refine = true
  Tool = -> Extrude045
note: 1 file-system path scrubbed to <path> (originals preserved in the JSON sidecar)
